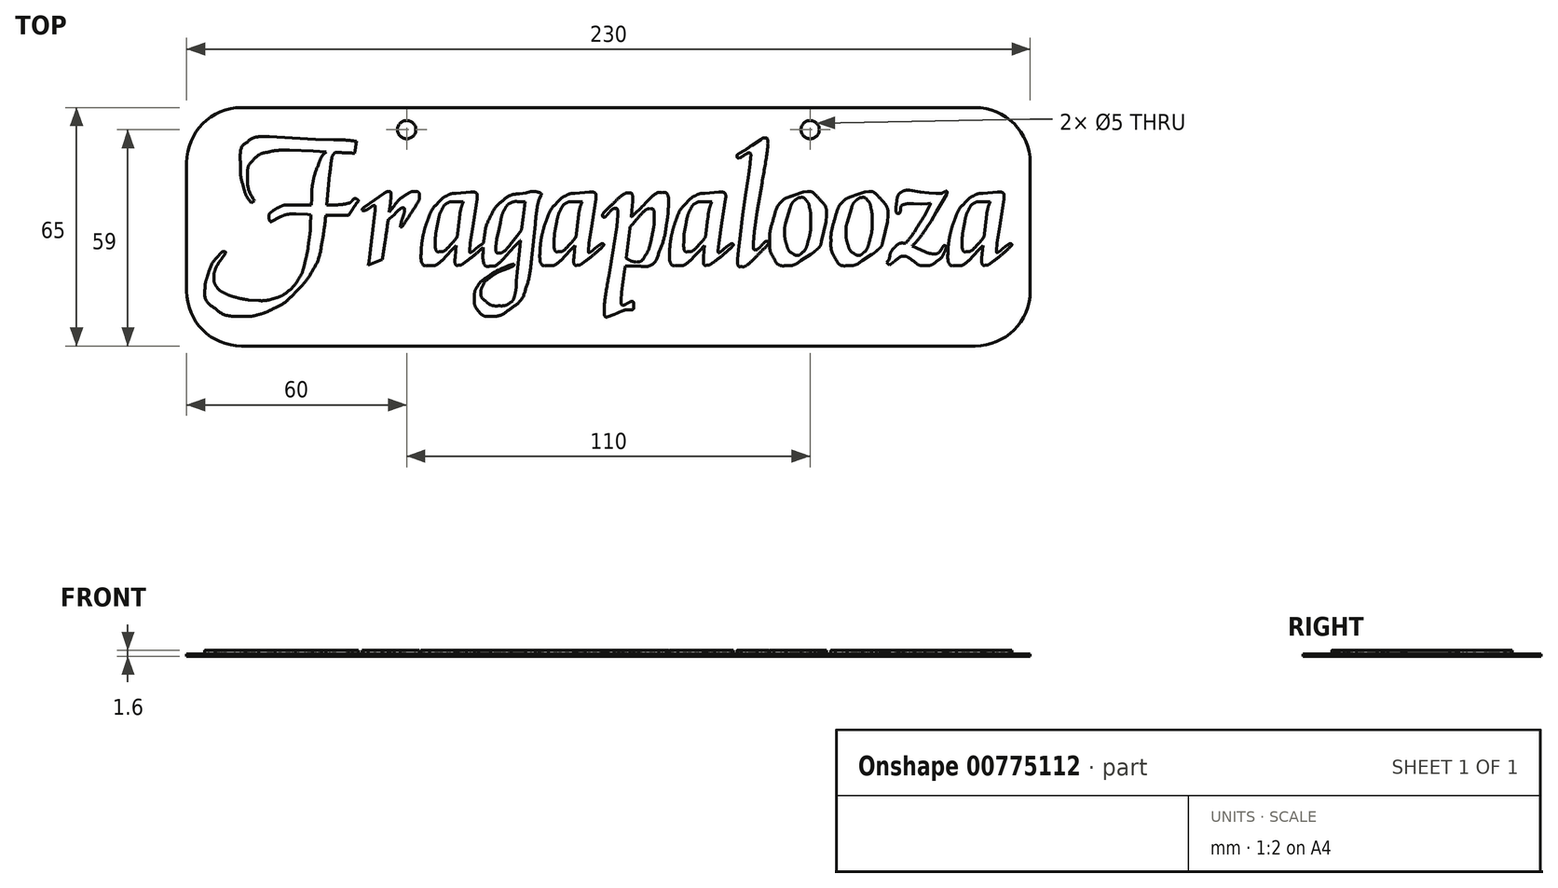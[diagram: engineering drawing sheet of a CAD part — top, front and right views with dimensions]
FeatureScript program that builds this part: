
annotation { "Feature Type Name" : "Feature", "Feature Type Description" : "" }
export const myFeature = defineFeature(function(context is Context, id is Id, definition is map)
    precondition{}
    {
        {
            var Q0;
            Q0=qCreatedBy(makeId("Top.planeOp"),FACE);
            var sketch = newSketch(context, id + "F0", { "sketchPlane" : qUnion([Q0])});
            skLineSegment(sketch, "E0.bottom", {"start": v(-100, 32.5) * mm, "end": v(100, 32.5) * mm});
            skLineSegment(sketch, "E0.top", {"start": v(-100, -32.5) * mm, "end": v(100, -32.5) * mm});
            skLineSegment(sketch, "E0.left", {"start": v(-115, 17.5) * mm, "end": v(-115, -17.5) * mm});
            skLineSegment(sketch, "E0.right", {"start": v(115, 17.5) * mm, "end": v(115, -17.5) * mm});
            skPoint(sketch, "E0.middle", {"position": v(0, 0) * mm});
            skPoint(sketch, "E1.visualSharp", {"position": v(-115, 32.5) * mm});
            skArc(sketch, "E1.filletArc", {"start": v(-100, 32.5) * mm, "mid": v(-110.6, 28.1) * mm, "end": v(-115, 17.5) * mm});
            skPoint(sketch, "E2.visualSharp", {"position": v(115, 32.5) * mm});
            skArc(sketch, "E2.filletArc", {"start": v(115, 17.5) * mm, "mid": v(110.6, 28.1) * mm, "end": v(100, 32.5) * mm});
            skPoint(sketch, "E3.visualSharp", {"position": v(115, -32.5) * mm});
            skArc(sketch, "E3.filletArc", {"start": v(100, -32.5) * mm, "mid": v(110.6, -28.1) * mm, "end": v(115, -17.5) * mm});
            skPoint(sketch, "E4.visualSharp", {"position": v(-115, -32.5) * mm});
            skArc(sketch, "E4.filletArc", {"start": v(-115, -17.5) * mm, "mid": v(-110.6, -28.1) * mm, "end": v(-100, -32.5) * mm});
            skCircle(sketch, "E5", {"center": v(-55, 26.5) * mm, "radius": 2.5 * mm});
            skCircle(sketch, "E6", {"center": v(55, 26.5) * mm, "radius": 2.5 * mm});
            skLineSegment(sketch, "E7", {"start": v(-55, 26.5) * mm, "end": v(0, 26.5) * mm, "construction": true});
            skLineSegment(sketch, "E8", {"start": v(0, 26.5) * mm, "end": v(55, 26.5) * mm, "construction": true});
            skSolve(sketch);
        }
        {
            var Q0;
            Q0=makeQuery(id+"F0.imprint","IMPRINT",FACE,{"disambiguationData":[TD([[makeQuery(id+"F0.imprint","IMPRINT",EDGE,{"derivedFrom":sQuery(id+"F0.wireOp",EDGE,"E0.bottom")}),-1.0]])]});
            extrude(context, id + "F1", {"entities" : qUnion([Q0]), "depth" : .6 * mm, "offsetDistance" : 25 * mm});
        }
        {
            var Q0;
            Q0=makeQuery(id+"F1.opExtrude","CAP_FACE",FACE,{"disambiguationData":[OSD([sQuery(id+"F0.wireOp",EDGE,"E0.bottom"),sQuery(id+"F0.wireOp",EDGE,"E0.top"),sQuery(id+"F0.wireOp",EDGE,"E0.left"),sQuery(id+"F0.wireOp",EDGE,"E0.right")])],"isStart":false});
            var sketch = newSketch(context, id + "F2", { "sketchPlane" : qUnion([Q0])});
            skLineSegment(sketch, "E9", {"start": v(-92.11, 1.33) * mm, "end": v(-89.44, 2.74) * mm});
            skLineSegment(sketch, "E10", {"start": v(-85.15, 3.5) * mm, "end": v(-82, 3.36) * mm});
            skLineSegment(sketch, "E11", {"start": v(-82, 3.36) * mm, "end": v(-78.73, 3.18) * mm});
            skLineSegment(sketch, "E12", {"start": v(-78.73, 3.18) * mm, "end": v(-70.78, 3.18) * mm});
            skLineSegment(sketch, "E13", {"start": v(-70.78, 3.18) * mm, "end": v(-69.8, 4.65) * mm});
            skLineSegment(sketch, "E14", {"start": v(-68.12, 7.04) * mm, "end": v(-68.17, 7.2) * mm});
            skLineSegment(sketch, "E15", {"start": v(-77.15, 5.95) * mm, "end": v(-80.41, 5.95) * mm});
            skLineSegment(sketch, "E16", {"start": v(-80.41, 5.95) * mm, "end": v(-84.55, 5.95) * mm});
            skLineSegment(sketch, "E17", {"start": v(-84.55, 5.95) * mm, "end": v(-87.87, 5.95) * mm});
            skLineSegment(sketch, "E18", {"start": v(-86.92, 20.9) * mm, "end": v(-80.51, 20.63) * mm});
            skLineSegment(sketch, "E19", {"start": v(-80.51, 20.63) * mm, "end": v(-74.61, 20.25) * mm});
            skLineSegment(sketch, "E20", {"start": v(-69.22, 20.03) * mm, "end": v(-68.67, 23.34) * mm});
            skLineSegment(sketch, "E21", {"start": v(-74.87, 23.74) * mm, "end": v(-79.85, 23.85) * mm});
            skLineSegment(sketch, "E22", {"start": v(-79.85, 23.85) * mm, "end": v(-86.2, 24.25) * mm});
            skLineSegment(sketch, "E23", {"start": v(-86.2, 24.25) * mm, "end": v(-92.4, 24.56) * mm});
            skLineSegment(sketch, "E24", {"start": v(-97.4, 6.61) * mm, "end": v(-96.48, 7.12) * mm});
            skLineSegment(sketch, "E25", {"start": v(-76.95, 4.81) * mm, "end": v(-75.99, 14.38) * mm});
            skLineSegment(sketch, "E26", {"start": v(-75.12, 19.57) * mm, "end": v(-74.46, 20.29) * mm});
            skLineSegment(sketch, "E27", {"start": v(-74.15, 21.15) * mm, "end": v(-75.12, 20.95) * mm});
            skLineSegment(sketch, "E28", {"start": v(-80.92, 7.78) * mm, "end": v(-81.22, 0.56) * mm});
            skLineSegment(sketch, "E29", {"start": v(-95.36, -20.13) * mm, "end": v(-98.05, -19.93) * mm});
            skLineSegment(sketch, "E30", {"start": v(-105.53, -8.84) * mm, "end": v(-104.56, -7.57) * mm});
            skLineSegment(sketch, "E31", {"start": v(-104.56, -7.57) * mm, "end": v(-104.4, -7.17) * mm});
            skLineSegment(sketch, "E32", {"start": v(-59.4, 6.55) * mm, "end": v(-59.26, 8.23) * mm});
            skLineSegment(sketch, "E33", {"start": v(-61.19, 9.15) * mm, "end": v(-63.78, 7.35) * mm});
            skLineSegment(sketch, "E34", {"start": v(-63.78, 7.35) * mm, "end": v(-66.68, 5.3) * mm});
            skLineSegment(sketch, "E35", {"start": v(-67.09, 4.53) * mm, "end": v(-66.88, 4.42) * mm});
            skLineSegment(sketch, "E36", {"start": v(-66.88, 4.42) * mm, "end": v(-66.58, 4.47) * mm});
            skLineSegment(sketch, "E37", {"start": v(-66.58, 4.47) * mm, "end": v(-66.27, 4.53) * mm});
            skLineSegment(sketch, "E38", {"start": v(-63.58, 4.53) * mm, "end": v(-64.6, -3.97) * mm});
            skLineSegment(sketch, "E39", {"start": v(-64.6, -3.97) * mm, "end": v(-65.26, -9.46) * mm});
            skLineSegment(sketch, "E40", {"start": v(-65.51, -10.42) * mm, "end": v(-61.65, -8.94) * mm});
            skLineSegment(sketch, "E41", {"start": v(-58.44, 5.7) * mm, "end": v(-60.27, 3.36) * mm});
            skLineSegment(sketch, "E42", {"start": v(-59.66, 2.24) * mm, "end": v(-58.44, 3.3) * mm});
            skLineSegment(sketch, "E43", {"start": v(-39.33, 6.88) * mm, "end": v(-38, 6.88) * mm});
            skLineSegment(sketch, "E44", {"start": v(-38, 6.88) * mm, "end": v(-37.04, 7.08) * mm});
            skLineSegment(sketch, "E45", {"start": v(-37.6, 9.47) * mm, "end": v(-41.46, 9.11) * mm});
            skLineSegment(sketch, "E46", {"start": v(-42.99, -6.63) * mm, "end": v(-41.26, -4.74) * mm});
            skLineSegment(sketch, "E47", {"start": v(-39.63, -0.7) * mm, "end": v(-40.8, -2.13) * mm});
            skLineSegment(sketch, "E48", {"start": v(-42.12, 6.88) * mm, "end": v(-40.9, 6.88) * mm});
            skLineSegment(sketch, "E49", {"start": v(-40.9, 6.88) * mm, "end": v(-39.33, 6.88) * mm});
            skLineSegment(sketch, "E50", {"start": v(-40.59, 2.44) * mm, "end": v(-41.18, -1.98) * mm});
            skLineSegment(sketch, "E51", {"start": v(-41.18, -1.98) * mm, "end": v(-41.68, -6.2) * mm});
            skLineSegment(sketch, "E52", {"start": v(-41.68, -6.2) * mm, "end": v(-41.82, -8.6) * mm});
            skLineSegment(sketch, "E53", {"start": v(-36.58, -6.36) * mm, "end": v(-37.65, -7.12) * mm});
            skLineSegment(sketch, "E54", {"start": v(-37.85, -6.5) * mm, "end": v(-37.65, -4.42) * mm});
            skLineSegment(sketch, "E55", {"start": v(-37.65, -4.42) * mm, "end": v(-36.8, 1.02) * mm});
            skLineSegment(sketch, "E56", {"start": v(-36.8, 1.02) * mm, "end": v(-35.78, 7.58) * mm});
            skLineSegment(sketch, "E57", {"start": v(-21.58, 6.88) * mm, "end": v(-20.28, 6.88) * mm});
            skLineSegment(sketch, "E58", {"start": v(-20.28, 6.88) * mm, "end": v(-19.33, 7.12) * mm});
            skLineSegment(sketch, "E59", {"start": v(-18.74, 7.75) * mm, "end": v(-18.33, 8.63) * mm});
            skLineSegment(sketch, "E60", {"start": v(-19.85, 9.65) * mm, "end": v(-21.12, 9.65) * mm});
            skLineSegment(sketch, "E61", {"start": v(-21.12, 9.65) * mm, "end": v(-22.45, 9.2) * mm});
            skLineSegment(sketch, "E62", {"start": v(-22.45, 9.2) * mm, "end": v(-24.23, 9) * mm});
            skLineSegment(sketch, "E63", {"start": v(-27.23, -7.1) * mm, "end": v(-25.1, -4.86) * mm});
            skLineSegment(sketch, "E64", {"start": v(-23.06, -0.05) * mm, "end": v(-24.84, -2.4) * mm});
            skLineSegment(sketch, "E65", {"start": v(-24.84, -2.4) * mm, "end": v(-26.87, -5.02) * mm});
            skLineSegment(sketch, "E66", {"start": v(-30.68, -5.5) * mm, "end": v(-30.48, -3.38) * mm});
            skLineSegment(sketch, "E67", {"start": v(-30.48, -3.38) * mm, "end": v(-29.87, -0.6) * mm});
            skLineSegment(sketch, "E68", {"start": v(-29.87, -0.6) * mm, "end": v(-29.46, 1.1) * mm});
            skLineSegment(sketch, "E69", {"start": v(-24.73, 6.88) * mm, "end": v(-23.26, 6.88) * mm});
            skLineSegment(sketch, "E70", {"start": v(-23.26, 6.88) * mm, "end": v(-21.58, 6.88) * mm});
            skLineSegment(sketch, "E71", {"start": v(-22.45, 8.37) * mm, "end": v(-23.27, 2.78) * mm});
            skLineSegment(sketch, "E72", {"start": v(-23.27, 2.78) * mm, "end": v(-24.16, -5.26) * mm});
            skLineSegment(sketch, "E73", {"start": v(-24.16, -5.26) * mm, "end": v(-24.77, -11.16) * mm});
            skLineSegment(sketch, "E74", {"start": v(-24.77, -11.16) * mm, "end": v(-25.1, -14.82) * mm});
            skLineSegment(sketch, "E75", {"start": v(-29.77, -12.22) * mm, "end": v(-27.07, -11.15) * mm});
            skLineSegment(sketch, "E76", {"start": v(-25.6, -10.4) * mm, "end": v(-25.7, -10.24) * mm});
            skLineSegment(sketch, "E77", {"start": v(-20.92, -8.56) * mm, "end": v(-19.96, 0.74) * mm});
            skLineSegment(sketch, "E78", {"start": v(-6.94, 6.88) * mm, "end": v(-5.62, 6.88) * mm});
            skLineSegment(sketch, "E79", {"start": v(-5.62, 6.88) * mm, "end": v(-4.65, 7.08) * mm});
            skLineSegment(sketch, "E80", {"start": v(-5.21, 9.47) * mm, "end": v(-9.08, 9.11) * mm});
            skLineSegment(sketch, "E81", {"start": v(-10.6, -6.63) * mm, "end": v(-8.87, -4.74) * mm});
            skLineSegment(sketch, "E82", {"start": v(-7.24, -0.7) * mm, "end": v(-8.41, -2.13) * mm});
            skLineSegment(sketch, "E83", {"start": v(-9.74, 6.88) * mm, "end": v(-8.52, 6.88) * mm});
            skLineSegment(sketch, "E84", {"start": v(-8.52, 6.88) * mm, "end": v(-6.94, 6.88) * mm});
            skLineSegment(sketch, "E85", {"start": v(-8.2, 2.44) * mm, "end": v(-8.79, -1.98) * mm});
            skLineSegment(sketch, "E86", {"start": v(-8.79, -1.98) * mm, "end": v(-9.3, -6.2) * mm});
            skLineSegment(sketch, "E87", {"start": v(-9.3, -6.2) * mm, "end": v(-9.43, -8.6) * mm});
            skLineSegment(sketch, "E88", {"start": v(-4.2, -6.36) * mm, "end": v(-5.26, -7.12) * mm});
            skLineSegment(sketch, "E89", {"start": v(-5.47, -6.5) * mm, "end": v(-5.26, -4.42) * mm});
            skLineSegment(sketch, "E90", {"start": v(-5.26, -4.42) * mm, "end": v(-4.4, 1.02) * mm});
            skLineSegment(sketch, "E91", {"start": v(-4.4, 1.02) * mm, "end": v(-3.4, 7.58) * mm});
            skLineSegment(sketch, "E92", {"start": v(2.52, 3.3) * mm, "end": v(2.26, 0.05) * mm});
            skLineSegment(sketch, "E93", {"start": v(2.26, 0.05) * mm, "end": v(1.43, -5.54) * mm});
            skLineSegment(sketch, "E94", {"start": v(1.43, -5.54) * mm, "end": v(0.12, -13.32) * mm});
            skLineSegment(sketch, "E95", {"start": v(-0.18, -24.56) * mm, "end": v(1.5, -23.95) * mm});
            skLineSegment(sketch, "E96", {"start": v(3.48, -20.03) * mm, "end": v(3.59, -17.84) * mm});
            skLineSegment(sketch, "E97", {"start": v(3.59, -17.84) * mm, "end": v(4.37, -12.25) * mm});
            skLineSegment(sketch, "E98", {"start": v(4.37, -12.25) * mm, "end": v(5.35, -4.47) * mm});
            skLineSegment(sketch, "E99", {"start": v(5.35, -4.47) * mm, "end": v(5.85, -0.35) * mm});
            skLineSegment(sketch, "E100", {"start": v(5.85, -0.35) * mm, "end": v(6.43, 4.42) * mm});
            skLineSegment(sketch, "E101", {"start": v(6.43, 4.42) * mm, "end": v(6.58, 6.97) * mm});
            skLineSegment(sketch, "E102", {"start": v(3.43, -8.96) * mm, "end": v(3.28, -9.48) * mm});
            skLineSegment(sketch, "E103", {"start": v(2.82, -10.68) * mm, "end": v(2.97, -10.82) * mm});
            skLineSegment(sketch, "E104", {"start": v(2.97, -10.82) * mm, "end": v(3.17, -10.9) * mm});
            skLineSegment(sketch, "E105", {"start": v(3.17, -10.9) * mm, "end": v(4.2, -10.7) * mm});
            skLineSegment(sketch, "E106", {"start": v(4.2, -10.7) * mm, "end": v(6.03, -10.7) * mm});
            skLineSegment(sketch, "E107", {"start": v(6.03, -10.7) * mm, "end": v(8.28, -10.7) * mm});
            skLineSegment(sketch, "E108", {"start": v(8.97, 5.25) * mm, "end": v(7.2, 3.56) * mm});
            skLineSegment(sketch, "E109", {"start": v(28.4, 6.88) * mm, "end": v(29.72, 6.88) * mm});
            skLineSegment(sketch, "E110", {"start": v(29.72, 6.88) * mm, "end": v(30.68, 7.08) * mm});
            skLineSegment(sketch, "E111", {"start": v(30.13, 9.47) * mm, "end": v(26.26, 9.11) * mm});
            skLineSegment(sketch, "E112", {"start": v(24.74, -6.63) * mm, "end": v(26.46, -4.74) * mm});
            skLineSegment(sketch, "E113", {"start": v(28.1, -0.7) * mm, "end": v(26.92, -2.13) * mm});
            skLineSegment(sketch, "E114", {"start": v(25.6, 6.88) * mm, "end": v(26.82, 6.88) * mm});
            skLineSegment(sketch, "E115", {"start": v(26.82, 6.88) * mm, "end": v(28.4, 6.88) * mm});
            skLineSegment(sketch, "E116", {"start": v(27.14, 2.44) * mm, "end": v(26.55, -1.98) * mm});
            skLineSegment(sketch, "E117", {"start": v(26.55, -1.98) * mm, "end": v(26.04, -6.2) * mm});
            skLineSegment(sketch, "E118", {"start": v(26.04, -6.2) * mm, "end": v(25.9, -8.6) * mm});
            skLineSegment(sketch, "E119", {"start": v(31.14, -6.36) * mm, "end": v(30.07, -7.12) * mm});
            skLineSegment(sketch, "E120", {"start": v(29.87, -6.5) * mm, "end": v(30.07, -4.42) * mm});
            skLineSegment(sketch, "E121", {"start": v(30.07, -4.42) * mm, "end": v(30.93, 1.02) * mm});
            skLineSegment(sketch, "E122", {"start": v(30.93, 1.02) * mm, "end": v(31.94, 7.58) * mm});
            skLineSegment(sketch, "E123", {"start": v(39.48, -4.47) * mm, "end": v(39.73, -1.27) * mm});
            skLineSegment(sketch, "E124", {"start": v(39.73, -1.27) * mm, "end": v(40.5, 4.12) * mm});
            skLineSegment(sketch, "E125", {"start": v(40.5, 4.12) * mm, "end": v(41.88, 12.05) * mm});
            skLineSegment(sketch, "E126", {"start": v(41.67, 23.9) * mm, "end": v(39.12, 22.22) * mm});
            skLineSegment(sketch, "E127", {"start": v(35.46, 18.76) * mm, "end": v(36.07, 18.97) * mm});
            skLineSegment(sketch, "E128", {"start": v(38.82, 19.07) * mm, "end": v(38.66, 17.14) * mm});
            skLineSegment(sketch, "E129", {"start": v(38.66, 17.14) * mm, "end": v(38.12, 13.47) * mm});
            skLineSegment(sketch, "E130", {"start": v(38.12, 13.47) * mm, "end": v(37.37, 8.65) * mm});
            skLineSegment(sketch, "E131", {"start": v(37.37, 8.65) * mm, "end": v(36.65, 3.26) * mm});
            skLineSegment(sketch, "E132", {"start": v(36.65, 3.26) * mm, "end": v(35.93, -2.13) * mm});
            skLineSegment(sketch, "E133", {"start": v(35.93, -2.13) * mm, "end": v(35.41, -6.36) * mm});
            skLineSegment(sketch, "E134", {"start": v(35.41, -6.36) * mm, "end": v(35.26, -8.8) * mm});
            skLineSegment(sketch, "E135", {"start": v(52.5, -9.2) * mm, "end": v(55.09, -7.53) * mm});
            skLineSegment(sketch, "E136", {"start": v(58.09, -3.98) * mm, "end": v(58.7, -1.24) * mm});
            skLineSegment(sketch, "E137", {"start": v(58.7, -1.24) * mm, "end": v(59.3, 1.34) * mm});
            skLineSegment(sketch, "E138", {"start": v(59.3, 1.34) * mm, "end": v(59.46, 3.12) * mm});
            skLineSegment(sketch, "E139", {"start": v(54.28, 9.6) * mm, "end": v(53.1, 9.46) * mm});
            skLineSegment(sketch, "E140", {"start": v(53.1, 9.46) * mm, "end": v(50.51, 8.6) * mm});
            skLineSegment(sketch, "E141", {"start": v(48.33, 0.97) * mm, "end": v(49.55, 5.19) * mm});
            skLineSegment(sketch, "E142", {"start": v(69.22, -9.2) * mm, "end": v(71.82, -7.53) * mm});
            skLineSegment(sketch, "E143", {"start": v(74.82, -3.98) * mm, "end": v(75.43, -1.24) * mm});
            skLineSegment(sketch, "E144", {"start": v(75.43, -1.24) * mm, "end": v(76.04, 1.34) * mm});
            skLineSegment(sketch, "E145", {"start": v(76.04, 1.34) * mm, "end": v(76.19, 3.12) * mm});
            skLineSegment(sketch, "E146", {"start": v(71, 9.6) * mm, "end": v(69.83, 9.46) * mm});
            skLineSegment(sketch, "E147", {"start": v(69.83, 9.46) * mm, "end": v(67.24, 8.6) * mm});
            skLineSegment(sketch, "E148", {"start": v(65.05, 0.97) * mm, "end": v(66.27, 5.19) * mm});
            skLineSegment(sketch, "E149", {"start": v(83.16, 6.3) * mm, "end": v(85.19, 6.2) * mm});
            skLineSegment(sketch, "E150", {"start": v(85.19, 6.2) * mm, "end": v(86.97, 6.3) * mm});
            skLineSegment(sketch, "E151", {"start": v(86.97, 6.3) * mm, "end": v(87.83, 6.4) * mm});
            skLineSegment(sketch, "E152", {"start": v(75.88, -9.6) * mm, "end": v(76.65, -10.42) * mm});
            skLineSegment(sketch, "E153", {"start": v(86.66, -0.4) * mm, "end": v(87.98, 1.68) * mm});
            skLineSegment(sketch, "E154", {"start": v(87.98, 1.68) * mm, "end": v(89.46, 4.17) * mm});
            skLineSegment(sketch, "E155", {"start": v(89.46, 4.17) * mm, "end": v(90.93, 6.76) * mm});
            skLineSegment(sketch, "E156", {"start": v(90.93, 6.76) * mm, "end": v(92.2, 8.9) * mm});
            skLineSegment(sketch, "E157", {"start": v(91.95, 9.71) * mm, "end": v(91.54, 9.56) * mm});
            skLineSegment(sketch, "E158", {"start": v(89.3, 9.1) * mm, "end": v(87.38, 9.2) * mm});
            skLineSegment(sketch, "E159", {"start": v(87.38, 9.2) * mm, "end": v(84.99, 9.5) * mm});
            skLineSegment(sketch, "E160", {"start": v(84.99, 9.5) * mm, "end": v(82.04, 9.97) * mm});
            skLineSegment(sketch, "E161", {"start": v(78.63, 7.07) * mm, "end": v(78.43, 5.34) * mm});
            skLineSegment(sketch, "E162", {"start": v(75.99, -9.56) * mm, "end": v(76.34, -10.02) * mm});
            skLineSegment(sketch, "E163", {"start": v(76.8, -10.27) * mm, "end": v(79.09, -8.5) * mm});
            skLineSegment(sketch, "E164", {"start": v(86.56, -6.92) * mm, "end": v(83.97, -5.75) * mm});
            skLineSegment(sketch, "E165", {"start": v(83.97, -5.75) * mm, "end": v(81.58, -4.63) * mm});
            skLineSegment(sketch, "E166", {"start": v(76.7, -7.98) * mm, "end": v(76.6, -8.54) * mm});
            skLineSegment(sketch, "E167", {"start": v(76.6, -8.54) * mm, "end": v(76.44, -9.05) * mm});
            skLineSegment(sketch, "E168", {"start": v(76.44, -9.05) * mm, "end": v(75.99, -9.56) * mm});
            skLineSegment(sketch, "E169", {"start": v(104.3, 6.88) * mm, "end": v(105.63, 6.88) * mm});
            skLineSegment(sketch, "E170", {"start": v(105.63, 6.88) * mm, "end": v(106.6, 7.08) * mm});
            skLineSegment(sketch, "E171", {"start": v(106.03, 9.47) * mm, "end": v(102.17, 9.11) * mm});
            skLineSegment(sketch, "E172", {"start": v(100.65, -6.63) * mm, "end": v(102.37, -4.74) * mm});
            skLineSegment(sketch, "E173", {"start": v(104, -0.7) * mm, "end": v(102.83, -2.13) * mm});
            skLineSegment(sketch, "E174", {"start": v(101.5, 6.88) * mm, "end": v(102.73, 6.88) * mm});
            skLineSegment(sketch, "E175", {"start": v(102.73, 6.88) * mm, "end": v(104.3, 6.88) * mm});
            skLineSegment(sketch, "E176", {"start": v(103.05, 2.44) * mm, "end": v(102.45, -1.98) * mm});
            skLineSegment(sketch, "E177", {"start": v(102.45, -1.98) * mm, "end": v(101.95, -6.2) * mm});
            skLineSegment(sketch, "E178", {"start": v(101.95, -6.2) * mm, "end": v(101.81, -8.6) * mm});
            skLineSegment(sketch, "E179", {"start": v(107.05, -6.36) * mm, "end": v(105.98, -7.12) * mm});
            skLineSegment(sketch, "E180", {"start": v(105.78, -6.5) * mm, "end": v(105.98, -4.42) * mm});
            skLineSegment(sketch, "E181", {"start": v(105.98, -4.42) * mm, "end": v(106.84, 1.02) * mm});
            skLineSegment(sketch, "E182", {"start": v(106.84, 1.02) * mm, "end": v(107.85, 7.58) * mm});
            skFitSpline(sketch, "E183", {"points": [v(-92.55, 2.47) * mm, v(-92.55, 2.22) * mm, v(-92.4, 1.83) * mm, v(-92.11, 1.33) * mm]});
            skFitSpline(sketch, "E184", {"points": [v(-89.44, 2.74) * mm, v(-88.14, 3.25) * mm, v(-86.7, 3.5) * mm, v(-85.15, 3.5) * mm]});
            skFitSpline(sketch, "E185", {"points": [v(-69.8, 4.65) * mm, v(-69.15, 5.73) * mm, v(-68.6, 6.53) * mm, v(-68.12, 7.04) * mm]});
            skFitSpline(sketch, "E186", {"points": [v(-68.17, 7.2) * mm, v(-68.2, 7.27) * mm, v(-68.32, 7.37) * mm, v(-68.5, 7.5) * mm]});
            skFitSpline(sketch, "E187", {"points": [v(-68.5, 7.5) * mm, v(-68.68, 7.63) * mm, v(-68.84, 7.7) * mm, v(-68.99, 7.7) * mm]});
            skFitSpline(sketch, "E188", {"points": [v(-68.99, 7.7) * mm, v(-69.28, 7.7) * mm, v(-69.58, 7.51) * mm, v(-69.89, 7.15) * mm]});
            skFitSpline(sketch, "E189", {"points": [v(-69.89, 7.15) * mm, v(-70.2, 6.78) * mm, v(-70.5, 6.55) * mm, v(-70.78, 6.44) * mm]});
            skFitSpline(sketch, "E190", {"points": [v(-70.78, 6.44) * mm, v(-72.7, 6.12) * mm, v(-74.83, 5.95) * mm, v(-77.15, 5.95) * mm]});
            skFitSpline(sketch, "E191", {"points": [v(-87.87, 5.95) * mm, v(-88.27, 5.95) * mm, v(-88.88, 5.77) * mm, v(-89.72, 5.4) * mm]});
            skFitSpline(sketch, "E192", {"points": [v(-89.72, 5.4) * mm, v(-90.62, 4.93) * mm, v(-91.33, 4.5) * mm, v(-91.84, 4.1) * mm]});
            skFitSpline(sketch, "E193", {"points": [v(-91.84, 4.1) * mm, v(-92.31, 3.74) * mm, v(-92.55, 3.2) * mm, v(-92.55, 2.47) * mm]});
            skFitSpline(sketch, "E194", {"points": [v(-96.48, 7.12) * mm, v(-97.73, 9.19) * mm, v(-98.36, 11.47) * mm, v(-98.36, 13.98) * mm]});
            skFitSpline(sketch, "E195", {"points": [v(-98.36, 13.98) * mm, v(-98.36, 15.71) * mm, v(-97.85, 17.12) * mm, v(-96.83, 18.2) * mm]});
            skFitSpline(sketch, "E196", {"points": [v(-96.83, 18.2) * mm, v(-95.81, 19.29) * mm, v(-94.5, 20) * mm, v(-92.9, 20.36) * mm]});
            skFitSpline(sketch, "E197", {"points": [v(-92.9, 20.36) * mm, v(-91.28, 20.72) * mm, v(-89.29, 20.9) * mm, v(-86.92, 20.9) * mm]});
            skFitSpline(sketch, "E198", {"points": [v(-74.61, 20.25) * mm, v(-73.53, 20.25) * mm, v(-72.48, 20.23) * mm, v(-71.46, 20.19) * mm]});
            skFitSpline(sketch, "E199", {"points": [v(-71.46, 20.19) * mm, v(-70.44, 20.14) * mm, v(-69.7, 20.1) * mm, v(-69.22, 20.03) * mm]});
            skFitSpline(sketch, "E200", {"points": [v(-68.67, 23.34) * mm, v(-71.04, 23.6) * mm, v(-73.1, 23.74) * mm, v(-74.87, 23.74) * mm]});
            skFitSpline(sketch, "E201", {"points": [v(-92.4, 24.56) * mm, v(-95.26, 24.56) * mm, v(-97.27, 24.07) * mm, v(-98.46, 23.08) * mm]});
            skFitSpline(sketch, "E202", {"points": [v(-98.46, 23.08) * mm, v(-99.71, 22.17) * mm, v(-100.34, 20.32) * mm, v(-100.34, 17.54) * mm]});
            skFitSpline(sketch, "E203", {"points": [v(-100.34, 17.54) * mm, v(-100.34, 15.1) * mm, v(-100.08, 12.96) * mm, v(-99.55, 11.1) * mm]});
            skFitSpline(sketch, "E204", {"points": [v(-99.55, 11.1) * mm, v(-99.03, 9.26) * mm, v(-98.3, 7.76) * mm, v(-97.4, 6.61) * mm]});
            skFitSpline(sketch, "E205", {"points": [v(-106.72, -8.36) * mm, v(-107.69, -9.46) * mm, v(-108.47, -10.92) * mm, v(-109.08, -12.74) * mm]});
            skFitSpline(sketch, "E206", {"points": [v(-109.08, -12.74) * mm, v(-109.7, -14.57) * mm, v(-110, -15.94) * mm, v(-110, -16.85) * mm]});
            skFitSpline(sketch, "E207", {"points": [v(-110, -16.85) * mm, v(-110, -19.05) * mm, v(-109.06, -20.86) * mm, v(-107.18, -22.28) * mm]});
            skFitSpline(sketch, "E208", {"points": [v(-107.18, -22.28) * mm, v(-105.3, -23.7) * mm, v(-102.53, -24.4) * mm, v(-98.87, -24.4) * mm]});
            skFitSpline(sketch, "E209", {"points": [v(-98.87, -24.4) * mm, v(-97.68, -24.4) * mm, v(-96.5, -24.24) * mm, v(-95.3, -23.9) * mm]});
            skFitSpline(sketch, "E210", {"points": [v(-95.3, -23.9) * mm, v(-94.12, -23.56) * mm, v(-92.65, -22.96) * mm, v(-90.88, -22.09) * mm]});
            skFitSpline(sketch, "E211", {"points": [v(-90.88, -22.09) * mm, v(-89.12, -21.22) * mm, v(-87.26, -19.8) * mm, v(-85.29, -17.79) * mm]});
            skFitSpline(sketch, "E212", {"points": [v(-85.29, -17.79) * mm, v(-83.32, -15.79) * mm, v(-81.77, -13.8) * mm, v(-80.64, -11.83) * mm]});
            skFitSpline(sketch, "E213", {"points": [v(-80.64, -11.83) * mm, v(-79.5, -9.87) * mm, v(-78.68, -7.46) * mm, v(-78.17, -4.63) * mm]});
            skFitSpline(sketch, "E214", {"points": [v(-78.17, -4.63) * mm, v(-77.66, -1.8) * mm, v(-77.26, 1.35) * mm, v(-76.95, 4.81) * mm]});
            skFitSpline(sketch, "E215", {"points": [v(-75.99, 14.38) * mm, v(-75.61, 17.44) * mm, v(-75.32, 19.17) * mm, v(-75.12, 19.57) * mm]});
            skFitSpline(sketch, "E216", {"points": [v(-74.46, 20.29) * mm, v(-74.22, 20.51) * mm, v(-74.08, 20.67) * mm, v(-74.03, 20.77) * mm]});
            skFitSpline(sketch, "E217", {"points": [v(-74.03, 20.77) * mm, v(-73.98, 20.86) * mm, v(-73.93, 20.96) * mm, v(-73.9, 21.06) * mm]});
            skFitSpline(sketch, "E218", {"points": [v(-73.9, 21.06) * mm, v(-74, 21.12) * mm, v(-74.09, 21.15) * mm, v(-74.15, 21.15) * mm]});
            skFitSpline(sketch, "E219", {"points": [v(-75.12, 20.95) * mm, v(-76.88, 20.44) * mm, v(-78.16, 19.2) * mm, v(-78.96, 17.24) * mm]});
            skFitSpline(sketch, "E220", {"points": [v(-78.96, 17.24) * mm, v(-79.76, 15.27) * mm, v(-80.28, 13.58) * mm, v(-80.54, 12.18) * mm]});
            skFitSpline(sketch, "E221", {"points": [v(-80.54, 12.18) * mm, v(-80.8, 10.77) * mm, v(-80.92, 9.3) * mm, v(-80.92, 7.78) * mm]});
            skFitSpline(sketch, "E222", {"points": [v(-81.22, 0.56) * mm, v(-81.22, -0.19) * mm, v(-81.26, -0.86) * mm, v(-81.32, -1.45) * mm]});
            skFitSpline(sketch, "E223", {"points": [v(-81.32, -1.45) * mm, v(-81.4, -2.04) * mm, v(-81.53, -2.97) * mm, v(-81.73, -4.22) * mm]});
            skFitSpline(sketch, "E224", {"points": [v(-81.73, -4.22) * mm, v(-81.93, -5.95) * mm, v(-82.26, -7.75) * mm, v(-82.72, -9.64) * mm]});
            skFitSpline(sketch, "E225", {"points": [v(-82.72, -9.64) * mm, v(-83.18, -11.52) * mm, v(-83.8, -13.1) * mm, v(-84.6, -14.39) * mm]});
            skFitSpline(sketch, "E226", {"points": [v(-84.6, -14.39) * mm, v(-85.4, -15.68) * mm, v(-86.36, -16.78) * mm, v(-87.48, -17.7) * mm]});
            skFitSpline(sketch, "E227", {"points": [v(-87.48, -17.7) * mm, v(-88.6, -18.5) * mm, v(-89.83, -19.12) * mm, v(-91.19, -19.52) * mm]});
            skFitSpline(sketch, "E228", {"points": [v(-91.19, -19.52) * mm, v(-92.54, -19.93) * mm, v(-93.93, -20.13) * mm, v(-95.36, -20.13) * mm]});
            skFitSpline(sketch, "E229", {"points": [v(-98.05, -19.93) * mm, v(-99.58, -19.7) * mm, v(-100.87, -19.42) * mm, v(-101.94, -19.12) * mm]});
            skFitSpline(sketch, "E230", {"points": [v(-101.94, -19.12) * mm, v(-103, -18.82) * mm, v(-103.97, -18.44) * mm, v(-104.84, -17.98) * mm]});
            skFitSpline(sketch, "E231", {"points": [v(-104.84, -17.98) * mm, v(-105.7, -17.53) * mm, v(-106.37, -16.94) * mm, v(-106.85, -16.23) * mm]});
            skFitSpline(sketch, "E232", {"points": [v(-106.85, -16.23) * mm, v(-107.32, -15.53) * mm, v(-107.56, -14.7) * mm, v(-107.56, -13.75) * mm]});
            skFitSpline(sketch, "E233", {"points": [v(-107.56, -13.75) * mm, v(-107.56, -13.11) * mm, v(-107.46, -12.48) * mm, v(-107.25, -11.85) * mm]});
            skFitSpline(sketch, "E234", {"points": [v(-107.25, -11.85) * mm, v(-107.05, -11.23) * mm, v(-106.8, -10.7) * mm, v(-106.5, -10.26) * mm]});
            skFitSpline(sketch, "E235", {"points": [v(-106.5, -10.26) * mm, v(-106.36, -9.95) * mm, v(-106.23, -9.73) * mm, v(-106.11, -9.57) * mm]});
            skFitSpline(sketch, "E236", {"points": [v(-106.11, -9.57) * mm, v(-106, -9.42) * mm, v(-105.8, -9.18) * mm, v(-105.53, -8.84) * mm]});
            skFitSpline(sketch, "E237", {"points": [v(-104.4, -7.17) * mm, v(-104.4, -6.86) * mm, v(-104.58, -6.71) * mm, v(-104.92, -6.71) * mm]});
            skFitSpline(sketch, "E238", {"points": [v(-104.92, -6.71) * mm, v(-105.15, -6.71) * mm, v(-105.76, -7.26) * mm, v(-106.72, -8.36) * mm]});
            skFitSpline(sketch, "E239", {"points": [v(-60.96, -4.51) * mm, v(-60.74, -3.01) * mm, v(-60.22, 0.67) * mm, v(-59.4, 6.55) * mm]});
            skFitSpline(sketch, "E240", {"points": [v(-59.26, 8.23) * mm, v(-59.26, 9.15) * mm, v(-59.48, 9.6) * mm, v(-59.92, 9.6) * mm]});
            skFitSpline(sketch, "E241", {"points": [v(-59.92, 9.6) * mm, v(-60.26, 9.6) * mm, v(-60.68, 9.46) * mm, v(-61.19, 9.15) * mm]});
            skFitSpline(sketch, "E242", {"points": [v(-66.68, 5.3) * mm, v(-66.95, 5.1) * mm, v(-67.09, 4.83) * mm, v(-67.09, 4.53) * mm]});
            skFitSpline(sketch, "E243", {"points": [v(-66.27, 4.53) * mm, v(-66, 4.6) * mm, v(-65.59, 4.82) * mm, v(-65.03, 5.21) * mm]});
            skFitSpline(sketch, "E244", {"points": [v(-65.03, 5.21) * mm, v(-64.47, 5.6) * mm, v(-64.09, 5.8) * mm, v(-63.88, 5.8) * mm]});
            skFitSpline(sketch, "E245", {"points": [v(-63.88, 5.8) * mm, v(-63.68, 5.8) * mm, v(-63.58, 5.37) * mm, v(-63.58, 4.53) * mm]});
            skFitSpline(sketch, "E246", {"points": [v(-65.26, -9.46) * mm, v(-65.3, -9.66) * mm, v(-65.33, -9.86) * mm, v(-65.38, -10.04) * mm]});
            skFitSpline(sketch, "E247", {"points": [v(-65.38, -10.04) * mm, v(-65.44, -10.23) * mm, v(-65.48, -10.36) * mm, v(-65.51, -10.42) * mm]});
            skFitSpline(sketch, "E248", {"points": [v(-61.65, -8.94) * mm, v(-61.41, -7.48) * mm, v(-61.18, -6) * mm, v(-60.96, -4.51) * mm]});
            skFitSpline(sketch, "E249", {"points": [v(-53.92, 3.57) * mm, v(-52.36, 5.99) * mm, v(-51.58, 7.5) * mm, v(-51.58, 8.12) * mm]});
            skFitSpline(sketch, "E250", {"points": [v(-51.58, 8.12) * mm, v(-51.58, 9.11) * mm, v(-52, 9.6) * mm, v(-52.85, 9.6) * mm]});
            skFitSpline(sketch, "E251", {"points": [v(-52.85, 9.6) * mm, v(-53.5, 9.6) * mm, v(-54.35, 9.26) * mm, v(-55.42, 8.57) * mm]});
            skFitSpline(sketch, "E252", {"points": [v(-55.42, 8.57) * mm, v(-56.49, 7.87) * mm, v(-57.5, 6.92) * mm, v(-58.44, 5.7) * mm]});
            skFitSpline(sketch, "E253", {"points": [v(-60.27, 3.36) * mm, v(-60.88, 3.08) * mm, v(-61.19, 2.64) * mm, v(-61.19, 2.03) * mm]});
            skFitSpline(sketch, "E254", {"points": [v(-61.19, 2.03) * mm, v(-61.19, 1.93) * mm, v(-61.1, 1.8) * mm, v(-60.94, 1.63) * mm]});
            skFitSpline(sketch, "E255", {"points": [v(-60.94, 1.63) * mm, v(-60.66, 1.63) * mm, v(-60.24, 1.83) * mm, v(-59.66, 2.24) * mm]});
            skFitSpline(sketch, "E256", {"points": [v(-58.44, 3.3) * mm, v(-57.26, 4.53) * mm, v(-56.43, 5.13) * mm, v(-55.95, 5.13) * mm]});
            skFitSpline(sketch, "E257", {"points": [v(-55.95, 5.13) * mm, v(-55.72, 5.13) * mm, v(-55.6, 4.97) * mm, v(-55.6, 4.63) * mm]});
            skFitSpline(sketch, "E258", {"points": [v(-55.6, 4.63) * mm, v(-55.6, 4.19) * mm, v(-55.74, 3.54) * mm, v(-56.03, 2.7) * mm]});
            skFitSpline(sketch, "E259", {"points": [v(-56.03, 2.7) * mm, v(-56.32, 1.85) * mm, v(-56.5, 1.24) * mm, v(-56.56, 0.86) * mm]});
            skFitSpline(sketch, "E260", {"points": [v(-56.56, 0.86) * mm, v(-56.63, 0.5) * mm, v(-56.68, 0.19) * mm, v(-56.71, -0.05) * mm]});
            skFitSpline(sketch, "E261", {"points": [v(-56.71, -0.05) * mm, v(-56.4, -0.05) * mm, v(-55.48, 1.16) * mm, v(-53.92, 3.57) * mm]});
            skFitSpline(sketch, "E262", {"points": [v(-37.04, 7.08) * mm, v(-36.77, 7.22) * mm, v(-36.54, 7.45) * mm, v(-36.35, 7.78) * mm]});
            skFitSpline(sketch, "E263", {"points": [v(-36.35, 7.78) * mm, v(-36.17, 8.11) * mm, v(-36.07, 8.42) * mm, v(-36.07, 8.7) * mm]});
            skFitSpline(sketch, "E264", {"points": [v(-36.07, 8.7) * mm, v(-36.07, 9.2) * mm, v(-36.58, 9.47) * mm, v(-37.6, 9.47) * mm]});
            skFitSpline(sketch, "E265", {"points": [v(-41.46, 9.11) * mm, v(-42.38, 9.11) * mm, v(-43.24, 8.9) * mm, v(-44.06, 8.48) * mm]});
            skFitSpline(sketch, "E266", {"points": [v(-44.06, 8.48) * mm, v(-44.87, 8.05) * mm, v(-45.77, 7.3) * mm, v(-46.75, 6.24) * mm]});
            skFitSpline(sketch, "E267", {"points": [v(-46.75, 6.24) * mm, v(-47.73, 5.17) * mm, v(-48.5, 3.92) * mm, v(-49.04, 2.48) * mm]});
            skFitSpline(sketch, "E268", {"points": [v(-49.04, 2.48) * mm, v(-49.58, 1.04) * mm, v(-49.97, -0.14) * mm, v(-50.2, -1.06) * mm]});
            skFitSpline(sketch, "E269", {"points": [v(-50.2, -1.06) * mm, v(-50.44, -1.97) * mm, v(-50.62, -2.8) * mm, v(-50.74, -3.55) * mm]});
            skFitSpline(sketch, "E270", {"points": [v(-50.74, -3.55) * mm, v(-50.86, -4.3) * mm, v(-50.94, -4.91) * mm, v(-50.97, -5.4) * mm]});
            skFitSpline(sketch, "E271", {"points": [v(-50.97, -5.4) * mm, v(-51, -5.9) * mm, v(-51.02, -6.26) * mm, v(-51.02, -6.5) * mm]});
            skFitSpline(sketch, "E272", {"points": [v(-51.02, -6.5) * mm, v(-51.02, -9.17) * mm, v(-50.28, -10.51) * mm, v(-48.78, -10.51) * mm]});
            skFitSpline(sketch, "E273", {"points": [v(-48.78, -10.51) * mm, v(-47.4, -10.51) * mm, v(-45.46, -9.22) * mm, v(-42.99, -6.63) * mm]});
            skFitSpline(sketch, "E274", {"points": [v(-41.26, -4.74) * mm, v(-40.72, -4.2) * mm, v(-40.28, -3.63) * mm, v(-39.94, -3.05) * mm]});
            skFitSpline(sketch, "E275", {"points": [v(-39.94, -3.05) * mm, v(-39.6, -2.47) * mm, v(-39.43, -1.9) * mm, v(-39.43, -1.31) * mm]});
            skFitSpline(sketch, "E276", {"points": [v(-39.43, -1.31) * mm, v(-39.43, -1.14) * mm, v(-39.5, -0.94) * mm, v(-39.63, -0.7) * mm]});
            skFitSpline(sketch, "E277", {"points": [v(-40.8, -2.13) * mm, v(-41.51, -3.13) * mm, v(-42.36, -4.14) * mm, v(-43.34, -5.19) * mm]});
            skFitSpline(sketch, "E278", {"points": [v(-43.34, -5.19) * mm, v(-44.33, -6.23) * mm, v(-45.17, -6.75) * mm, v(-45.88, -6.75) * mm]});
            skFitSpline(sketch, "E279", {"points": [v(-45.88, -6.75) * mm, v(-46.73, -6.75) * mm, v(-47.16, -5.85) * mm, v(-47.16, -4.05) * mm]});
            skFitSpline(sketch, "E280", {"points": [v(-47.16, -4.05) * mm, v(-47.16, -2.8) * mm, v(-46.98, -1.25) * mm, v(-46.62, 0.6) * mm]});
            skFitSpline(sketch, "E281", {"points": [v(-46.62, 0.6) * mm, v(-46.27, 2.44) * mm, v(-45.86, 3.8) * mm, v(-45.4, 4.69) * mm]});
            skFitSpline(sketch, "E282", {"points": [v(-45.4, 4.69) * mm, v(-44.94, 5.57) * mm, v(-44.45, 6.16) * mm, v(-43.93, 6.44) * mm]});
            skFitSpline(sketch, "E283", {"points": [v(-43.93, 6.44) * mm, v(-43.4, 6.73) * mm, v(-42.8, 6.88) * mm, v(-42.12, 6.88) * mm]});
            skFitSpline(sketch, "E284", {"points": [v(-35.78, 7.58) * mm, v(-35.78, 8.76) * mm, v(-36.15, 9.36) * mm, v(-36.9, 9.36) * mm]});
            skFitSpline(sketch, "E285", {"points": [v(-36.9, 9.36) * mm, v(-37.3, 9.36) * mm, v(-37.79, 9.12) * mm, v(-38.36, 8.64) * mm]});
            skFitSpline(sketch, "E286", {"points": [v(-38.36, 8.64) * mm, v(-38.87, 8.13) * mm, v(-39.28, 7.48) * mm, v(-39.6, 6.68) * mm]});
            skFitSpline(sketch, "E287", {"points": [v(-39.6, 6.68) * mm, v(-39.92, 5.89) * mm, v(-40.15, 5.2) * mm, v(-40.28, 4.6) * mm]});
            skFitSpline(sketch, "E288", {"points": [v(-40.28, 4.6) * mm, v(-40.42, 4) * mm, v(-40.52, 3.29) * mm, v(-40.59, 2.44) * mm]});
            skFitSpline(sketch, "E289", {"points": [v(-41.82, -8.6) * mm, v(-41.82, -9.85) * mm, v(-41.53, -10.47) * mm, v(-40.95, -10.47) * mm]});
            skFitSpline(sketch, "E290", {"points": [v(-40.95, -10.47) * mm, v(-40.41, -10.47) * mm, v(-39.67, -10.1) * mm, v(-38.72, -9.36) * mm]});
            skFitSpline(sketch, "E291", {"points": [v(-38.72, -9.36) * mm, v(-37.77, -8.71) * mm, v(-36.22, -7.44) * mm, v(-34.09, -5.54) * mm]});
            skFitSpline(sketch, "E292", {"points": [v(-34.09, -5.54) * mm, v(-33.95, -5.37) * mm, v(-33.85, -5.24) * mm, v(-33.78, -5.13) * mm]});
            skFitSpline(sketch, "E293", {"points": [v(-33.78, -5.13) * mm, v(-33.72, -5.03) * mm, v(-33.67, -4.93) * mm, v(-33.63, -4.83) * mm]});
            skFitSpline(sketch, "E294", {"points": [v(-33.63, -4.83) * mm, v(-33.63, -4.76) * mm, v(-33.72, -4.68) * mm, v(-33.89, -4.58) * mm]});
            skFitSpline(sketch, "E295", {"points": [v(-33.89, -4.58) * mm, v(-34.12, -4.58) * mm, v(-34.42, -4.7) * mm, v(-34.78, -4.93) * mm]});
            skFitSpline(sketch, "E296", {"points": [v(-34.78, -4.93) * mm, v(-35.13, -5.17) * mm, v(-35.46, -5.4) * mm, v(-35.77, -5.64) * mm]});
            skFitSpline(sketch, "E297", {"points": [v(-35.77, -5.64) * mm, v(-36.07, -5.88) * mm, v(-36.34, -6.12) * mm, v(-36.58, -6.36) * mm]});
            skFitSpline(sketch, "E298", {"points": [v(-37.65, -7.12) * mm, v(-37.68, -7.09) * mm, v(-37.72, -7.03) * mm, v(-37.77, -6.94) * mm]});
            skFitSpline(sketch, "E299", {"points": [v(-37.77, -6.94) * mm, v(-37.83, -6.86) * mm, v(-37.85, -6.71) * mm, v(-37.85, -6.5) * mm]});
            skFitSpline(sketch, "E300", {"points": [v(-19.33, 7.12) * mm, v(-19.07, 7.3) * mm, v(-18.87, 7.5) * mm, v(-18.74, 7.75) * mm]});
            skFitSpline(sketch, "E301", {"points": [v(-18.33, 8.63) * mm, v(-18.33, 9.11) * mm, v(-18.84, 9.36) * mm, v(-19.85, 9.65) * mm]});
            skFitSpline(sketch, "E302", {"points": [v(-24.23, 9) * mm, v(-25.99, 8.83) * mm, v(-27.52, 8.2) * mm, v(-28.83, 7.11) * mm]});
            skFitSpline(sketch, "E303", {"points": [v(-28.83, 7.11) * mm, v(-30.13, 6.02) * mm, v(-31.2, 4.65) * mm, v(-32.06, 2.98) * mm]});
            skFitSpline(sketch, "E304", {"points": [v(-32.06, 2.98) * mm, v(-32.9, 1.32) * mm, v(-33.46, -0.38) * mm, v(-33.73, -2.11) * mm]});
            skFitSpline(sketch, "E305", {"points": [v(-33.73, -2.11) * mm, v(-34, -3.85) * mm, v(-34.14, -5.33) * mm, v(-34.14, -6.55) * mm]});
            skFitSpline(sketch, "E306", {"points": [v(-34.14, -6.55) * mm, v(-34.14, -9.3) * mm, v(-33.48, -10.68) * mm, v(-32.16, -10.68) * mm]});
            skFitSpline(sketch, "E307", {"points": [v(-32.16, -10.68) * mm, v(-31.04, -10.68) * mm, v(-29.4, -9.49) * mm, v(-27.23, -7.1) * mm]});
            skFitSpline(sketch, "E308", {"points": [v(-25.1, -4.86) * mm, v(-24.41, -4.14) * mm, v(-23.9, -3.6) * mm, v(-23.57, -3.22) * mm]});
            skFitSpline(sketch, "E309", {"points": [v(-23.57, -3.22) * mm, v(-23.23, -2.85) * mm, v(-22.88, -2.4) * mm, v(-22.52, -1.87) * mm]});
            skFitSpline(sketch, "E310", {"points": [v(-22.52, -1.87) * mm, v(-22.17, -1.34) * mm, v(-21.99, -0.79) * mm, v(-21.99, -0.2) * mm]});
            skFitSpline(sketch, "E311", {"points": [v(-21.99, -0.2) * mm, v(-21.99, 0.27) * mm, v(-22.1, 0.5) * mm, v(-22.3, 0.5) * mm]});
            skFitSpline(sketch, "E312", {"points": [v(-22.3, 0.5) * mm, v(-22.5, 0.5) * mm, v(-22.75, 0.32) * mm, v(-23.06, -0.05) * mm]});
            skFitSpline(sketch, "E313", {"points": [v(-26.87, -5.02) * mm, v(-28.2, -6.42) * mm, v(-29.18, -7.12) * mm, v(-29.82, -7.12) * mm]});
            skFitSpline(sketch, "E314", {"points": [v(-29.82, -7.12) * mm, v(-30.4, -7.12) * mm, v(-30.68, -6.58) * mm, v(-30.68, -5.5) * mm]});
            skFitSpline(sketch, "E315", {"points": [v(-29.46, 1.1) * mm, v(-29.16, 2.66) * mm, v(-28.76, 3.88) * mm, v(-28.27, 4.77) * mm]});
            skFitSpline(sketch, "E316", {"points": [v(-28.27, 4.77) * mm, v(-27.78, 5.66) * mm, v(-27.24, 6.24) * mm, v(-26.67, 6.5) * mm]});
            skFitSpline(sketch, "E317", {"points": [v(-26.67, 6.5) * mm, v(-26.1, 6.78) * mm, v(-25.45, 6.91) * mm, v(-24.73, 6.88) * mm]});
            skFitSpline(sketch, "E318", {"points": [v(-20.46, 8.73) * mm, v(-20.77, 8.73) * mm, v(-21.2, 8.73) * mm, v(-21.79, 8.73) * mm]});
            skFitSpline(sketch, "E319", {"points": [v(-21.79, 8.73) * mm, v(-22.23, 8.73) * mm, v(-22.45, 8.6) * mm, v(-22.45, 8.37) * mm]});
            skFitSpline(sketch, "E320", {"points": [v(-25.1, -14.82) * mm, v(-25.1, -15.73) * mm, v(-25.14, -16.5) * mm, v(-25.24, -17.13) * mm]});
            skFitSpline(sketch, "E321", {"points": [v(-25.24, -17.13) * mm, v(-25.34, -17.76) * mm, v(-25.48, -18.4) * mm, v(-25.65, -19.04) * mm]});
            skFitSpline(sketch, "E322", {"points": [v(-25.65, -19.04) * mm, v(-25.92, -19.81) * mm, v(-26.36, -20.4) * mm, v(-26.97, -20.76) * mm]});
            skFitSpline(sketch, "E323", {"points": [v(-26.97, -20.76) * mm, v(-27.65, -21.27) * mm, v(-28.63, -21.53) * mm, v(-29.92, -21.53) * mm]});
            skFitSpline(sketch, "E324", {"points": [v(-29.92, -21.53) * mm, v(-31.2, -21.53) * mm, v(-32.34, -21.15) * mm, v(-33.3, -20.38) * mm]});
            skFitSpline(sketch, "E325", {"points": [v(-33.3, -20.38) * mm, v(-34.27, -19.62) * mm, v(-34.75, -18.73) * mm, v(-34.75, -17.71) * mm]});
            skFitSpline(sketch, "E326", {"points": [v(-34.75, -17.71) * mm, v(-34.75, -17.3) * mm, v(-34.6, -16.76) * mm, v(-34.27, -16.06) * mm]});
            skFitSpline(sketch, "E327", {"points": [v(-34.27, -16.06) * mm, v(-33.95, -15.37) * mm, v(-33.42, -14.73) * mm, v(-32.7, -14.15) * mm]});
            skFitSpline(sketch, "E328", {"points": [v(-32.7, -14.15) * mm, v(-31.96, -13.58) * mm, v(-31.43, -13.18) * mm, v(-31.1, -12.96) * mm]});
            skFitSpline(sketch, "E329", {"points": [v(-31.1, -12.96) * mm, v(-30.75, -12.74) * mm, v(-30.31, -12.5) * mm, v(-29.77, -12.22) * mm]});
            skFitSpline(sketch, "E330", {"points": [v(-27.07, -11.15) * mm, v(-26.63, -10.98) * mm, v(-26.31, -10.85) * mm, v(-26.1, -10.75) * mm]});
            skFitSpline(sketch, "E331", {"points": [v(-26.1, -10.75) * mm, v(-25.9, -10.65) * mm, v(-25.73, -10.53) * mm, v(-25.6, -10.4) * mm]});
            skFitSpline(sketch, "E332", {"points": [v(-25.7, -10.24) * mm, v(-26.28, -10.24) * mm, v(-27.28, -10.56) * mm, v(-28.7, -11.2) * mm]});
            skFitSpline(sketch, "E333", {"points": [v(-28.7, -11.2) * mm, v(-30.12, -11.85) * mm, v(-31.52, -12.64) * mm, v(-32.9, -13.6) * mm]});
            skFitSpline(sketch, "E334", {"points": [v(-32.9, -13.6) * mm, v(-34.27, -14.54) * mm, v(-35.22, -15.46) * mm, v(-35.74, -16.34) * mm]});
            skFitSpline(sketch, "E335", {"points": [v(-35.74, -16.34) * mm, v(-36.27, -17.22) * mm, v(-36.53, -18.3) * mm, v(-36.53, -19.6) * mm]});
            skFitSpline(sketch, "E336", {"points": [v(-36.53, -19.6) * mm, v(-36.53, -20.88) * mm, v(-36.15, -22) * mm, v(-35.39, -22.95) * mm]});
            skFitSpline(sketch, "E337", {"points": [v(-35.39, -22.95) * mm, v(-34.62, -23.9) * mm, v(-33.55, -24.37) * mm, v(-32.16, -24.37) * mm]});
            skFitSpline(sketch, "E338", {"points": [v(-32.16, -24.37) * mm, v(-30.4, -24.37) * mm, v(-28.52, -23.65) * mm, v(-26.54, -22.19) * mm]});
            skFitSpline(sketch, "E339", {"points": [v(-26.54, -22.19) * mm, v(-24.56, -20.73) * mm, v(-23.22, -18.92) * mm, v(-22.52, -16.77) * mm]});
            skFitSpline(sketch, "E340", {"points": [v(-22.52, -16.77) * mm, v(-21.83, -14.62) * mm, v(-21.3, -11.88) * mm, v(-20.92, -8.56) * mm]});
            skFitSpline(sketch, "E341", {"points": [v(-19.96, 0.74) * mm, v(-19.65, 3.7) * mm, v(-19.24, 6.13) * mm, v(-18.74, 8.06) * mm]});
            skFitSpline(sketch, "E342", {"points": [v(-18.74, 8.06) * mm, v(-18.74, 8.5) * mm, v(-19.31, 8.73) * mm, v(-20.46, 8.73) * mm]});
            skFitSpline(sketch, "E343", {"points": [v(-4.65, 7.08) * mm, v(-4.38, 7.22) * mm, v(-4.15, 7.45) * mm, v(-3.97, 7.78) * mm]});
            skFitSpline(sketch, "E344", {"points": [v(-3.97, 7.78) * mm, v(-3.78, 8.11) * mm, v(-3.69, 8.42) * mm, v(-3.69, 8.7) * mm]});
            skFitSpline(sketch, "E345", {"points": [v(-3.69, 8.7) * mm, v(-3.69, 9.2) * mm, v(-4.2, 9.47) * mm, v(-5.21, 9.47) * mm]});
            skFitSpline(sketch, "E346", {"points": [v(-9.08, 9.11) * mm, v(-10, 9.11) * mm, v(-10.86, 8.9) * mm, v(-11.67, 8.48) * mm]});
            skFitSpline(sketch, "E347", {"points": [v(-11.67, 8.48) * mm, v(-12.48, 8.05) * mm, v(-13.38, 7.3) * mm, v(-14.36, 6.24) * mm]});
            skFitSpline(sketch, "E348", {"points": [v(-14.36, 6.24) * mm, v(-15.35, 5.17) * mm, v(-16.1, 3.92) * mm, v(-16.65, 2.48) * mm]});
            skFitSpline(sketch, "E349", {"points": [v(-16.65, 2.48) * mm, v(-17.2, 1.04) * mm, v(-17.58, -0.14) * mm, v(-17.82, -1.06) * mm]});
            skFitSpline(sketch, "E350", {"points": [v(-17.82, -1.06) * mm, v(-18.06, -1.97) * mm, v(-18.24, -2.8) * mm, v(-18.35, -3.55) * mm]});
            skFitSpline(sketch, "E351", {"points": [v(-18.35, -3.55) * mm, v(-18.47, -4.3) * mm, v(-18.55, -4.91) * mm, v(-18.58, -5.4) * mm]});
            skFitSpline(sketch, "E352", {"points": [v(-18.58, -5.4) * mm, v(-18.62, -5.9) * mm, v(-18.63, -6.26) * mm, v(-18.63, -6.5) * mm]});
            skFitSpline(sketch, "E353", {"points": [v(-18.63, -6.5) * mm, v(-18.63, -9.17) * mm, v(-17.89, -10.51) * mm, v(-16.4, -10.51) * mm]});
            skFitSpline(sketch, "E354", {"points": [v(-16.4, -10.51) * mm, v(-15, -10.51) * mm, v(-13.07, -9.22) * mm, v(-10.6, -6.63) * mm]});
            skFitSpline(sketch, "E355", {"points": [v(-8.87, -4.74) * mm, v(-8.33, -4.2) * mm, v(-7.89, -3.63) * mm, v(-7.55, -3.05) * mm]});
            skFitSpline(sketch, "E356", {"points": [v(-7.55, -3.05) * mm, v(-7.21, -2.47) * mm, v(-7.04, -1.9) * mm, v(-7.04, -1.31) * mm]});
            skFitSpline(sketch, "E357", {"points": [v(-7.04, -1.31) * mm, v(-7.04, -1.14) * mm, v(-7.1, -0.94) * mm, v(-7.24, -0.7) * mm]});
            skFitSpline(sketch, "E358", {"points": [v(-8.41, -2.13) * mm, v(-9.13, -3.13) * mm, v(-9.97, -4.14) * mm, v(-10.96, -5.19) * mm]});
            skFitSpline(sketch, "E359", {"points": [v(-10.96, -5.19) * mm, v(-11.94, -6.23) * mm, v(-12.79, -6.75) * mm, v(-13.5, -6.75) * mm]});
            skFitSpline(sketch, "E360", {"points": [v(-13.5, -6.75) * mm, v(-14.35, -6.75) * mm, v(-14.77, -5.85) * mm, v(-14.77, -4.05) * mm]});
            skFitSpline(sketch, "E361", {"points": [v(-14.77, -4.05) * mm, v(-14.77, -2.8) * mm, v(-14.6, -1.25) * mm, v(-14.24, 0.6) * mm]});
            skFitSpline(sketch, "E362", {"points": [v(-14.24, 0.6) * mm, v(-13.88, 2.44) * mm, v(-13.47, 3.8) * mm, v(-13.02, 4.69) * mm]});
            skFitSpline(sketch, "E363", {"points": [v(-13.02, 4.69) * mm, v(-12.56, 5.57) * mm, v(-12.07, 6.16) * mm, v(-11.54, 6.44) * mm]});
            skFitSpline(sketch, "E364", {"points": [v(-11.54, 6.44) * mm, v(-11.02, 6.73) * mm, v(-10.41, 6.88) * mm, v(-9.74, 6.88) * mm]});
            skFitSpline(sketch, "E365", {"points": [v(-3.4, 7.58) * mm, v(-3.4, 8.76) * mm, v(-3.76, 9.36) * mm, v(-4.5, 9.36) * mm]});
            skFitSpline(sketch, "E366", {"points": [v(-4.5, 9.36) * mm, v(-4.91, 9.36) * mm, v(-5.4, 9.12) * mm, v(-5.97, 8.64) * mm]});
            skFitSpline(sketch, "E367", {"points": [v(-5.97, 8.64) * mm, v(-6.48, 8.13) * mm, v(-6.9, 7.48) * mm, v(-7.21, 6.68) * mm]});
            skFitSpline(sketch, "E368", {"points": [v(-7.21, 6.68) * mm, v(-7.53, 5.89) * mm, v(-7.76, 5.2) * mm, v(-7.9, 4.6) * mm]});
            skFitSpline(sketch, "E369", {"points": [v(-7.9, 4.6) * mm, v(-8.03, 4) * mm, v(-8.13, 3.29) * mm, v(-8.2, 2.44) * mm]});
            skFitSpline(sketch, "E370", {"points": [v(-9.43, -8.6) * mm, v(-9.43, -9.85) * mm, v(-9.14, -10.47) * mm, v(-8.57, -10.47) * mm]});
            skFitSpline(sketch, "E371", {"points": [v(-8.57, -10.47) * mm, v(-8.03, -10.47) * mm, v(-7.28, -10.1) * mm, v(-6.33, -9.36) * mm]});
            skFitSpline(sketch, "E372", {"points": [v(-6.33, -9.36) * mm, v(-5.38, -8.71) * mm, v(-3.84, -7.44) * mm, v(-1.7, -5.54) * mm]});
            skFitSpline(sketch, "E373", {"points": [v(-1.7, -5.54) * mm, v(-1.57, -5.37) * mm, v(-1.47, -5.24) * mm, v(-1.4, -5.13) * mm]});
            skFitSpline(sketch, "E374", {"points": [v(-1.4, -5.13) * mm, v(-1.33, -5.03) * mm, v(-1.28, -4.93) * mm, v(-1.24, -4.83) * mm]});
            skFitSpline(sketch, "E375", {"points": [v(-1.24, -4.83) * mm, v(-1.24, -4.76) * mm, v(-1.33, -4.68) * mm, v(-1.5, -4.58) * mm]});
            skFitSpline(sketch, "E376", {"points": [v(-1.5, -4.58) * mm, v(-1.74, -4.58) * mm, v(-2.03, -4.7) * mm, v(-2.39, -4.93) * mm]});
            skFitSpline(sketch, "E377", {"points": [v(-2.39, -4.93) * mm, v(-2.74, -5.17) * mm, v(-3.08, -5.4) * mm, v(-3.38, -5.64) * mm]});
            skFitSpline(sketch, "E378", {"points": [v(-3.38, -5.64) * mm, v(-3.69, -5.88) * mm, v(-3.96, -6.12) * mm, v(-4.2, -6.36) * mm]});
            skFitSpline(sketch, "E379", {"points": [v(-5.26, -7.12) * mm, v(-5.3, -7.09) * mm, v(-5.34, -7.03) * mm, v(-5.39, -6.94) * mm]});
            skFitSpline(sketch, "E380", {"points": [v(-5.39, -6.94) * mm, v(-5.44, -6.86) * mm, v(-5.47, -6.71) * mm, v(-5.47, -6.5) * mm]});
            skFitSpline(sketch, "E381", {"points": [v(0.15, 3.81) * mm, v(0.81, 4.6) * mm, v(1.4, 4.98) * mm, v(1.9, 4.98) * mm]});
            skFitSpline(sketch, "E382", {"points": [v(1.9, 4.98) * mm, v(2.31, 4.98) * mm, v(2.52, 4.42) * mm, v(2.52, 3.3) * mm]});
            skFitSpline(sketch, "E383", {"points": [v(0.12, -13.32) * mm, v(-0.69, -17.96) * mm, v(-1.1, -21.07) * mm, v(-1.1, -22.63) * mm]});
            skFitSpline(sketch, "E384", {"points": [v(-1.1, -22.63) * mm, v(-1.1, -23.91) * mm, v(-0.79, -24.56) * mm, v(-0.18, -24.56) * mm]});
            skFitSpline(sketch, "E385", {"points": [v(1.5, -23.95) * mm, v(2.04, -23.68) * mm, v(2.47, -23.47) * mm, v(2.8, -23.34) * mm]});
            skFitSpline(sketch, "E386", {"points": [v(2.8, -23.34) * mm, v(3.12, -23.2) * mm, v(3.5, -23.05) * mm, v(3.94, -22.88) * mm]});
            skFitSpline(sketch, "E387", {"points": [v(3.94, -22.88) * mm, v(4.38, -22.71) * mm, v(5.04, -22.63) * mm, v(5.92, -22.63) * mm]});
            skFitSpline(sketch, "E388", {"points": [v(5.92, -22.63) * mm, v(6.57, -22.63) * mm, v(6.9, -22.17) * mm, v(6.9, -21.25) * mm]});
            skFitSpline(sketch, "E389", {"points": [v(6.9, -21.25) * mm, v(6.9, -20.64) * mm, v(6.6, -20.34) * mm, v(6.03, -20.34) * mm]});
            skFitSpline(sketch, "E390", {"points": [v(6.03, -20.34) * mm, v(4.97, -20.98) * mm, v(4.31, -21.3) * mm, v(4.04, -21.3) * mm]});
            skFitSpline(sketch, "E391", {"points": [v(4.04, -21.3) * mm, v(3.67, -21.3) * mm, v(3.48, -20.88) * mm, v(3.48, -20.03) * mm]});
            skFitSpline(sketch, "E392", {"points": [v(6.58, 6.97) * mm, v(6.58, 8.46) * mm, v(6.26, 9.2) * mm, v(5.62, 9.2) * mm]});
            skFitSpline(sketch, "E393", {"points": [v(5.62, 9.2) * mm, v(4.7, 9.2) * mm, v(3.28, 8.28) * mm, v(1.35, 6.43) * mm]});
            skFitSpline(sketch, "E394", {"points": [v(1.35, 6.43) * mm, v(-0.58, 4.58) * mm, v(-1.55, 3.47) * mm, v(-1.55, 3.1) * mm]});
            skFitSpline(sketch, "E395", {"points": [v(-1.55, 3.1) * mm, v(-1.55, 2.8) * mm, v(-1.43, 2.64) * mm, v(-1.2, 2.64) * mm]});
            skFitSpline(sketch, "E396", {"points": [v(-1.2, 2.64) * mm, v(-0.96, 2.64) * mm, v(-0.5, 3.03) * mm, v(0.15, 3.81) * mm]});
            skFitSpline(sketch, "E397", {"points": [v(4.8, -8.5) * mm, v(4.53, -8.27) * mm, v(4.25, -8.15) * mm, v(3.94, -8.15) * mm]});
            skFitSpline(sketch, "E398", {"points": [v(3.94, -8.15) * mm, v(3.74, -8.19) * mm, v(3.6, -8.27) * mm, v(3.53, -8.41) * mm]});
            skFitSpline(sketch, "E399", {"points": [v(3.53, -8.41) * mm, v(3.47, -8.56) * mm, v(3.43, -8.74) * mm, v(3.43, -8.96) * mm]});
            skFitSpline(sketch, "E400", {"points": [v(3.28, -9.48) * mm, v(2.97, -10.02) * mm, v(2.82, -10.43) * mm, v(2.82, -10.68) * mm]});
            skFitSpline(sketch, "E401", {"points": [v(8.28, -10.7) * mm, v(10.95, -10.7) * mm, v(12.78, -9.46) * mm, v(13.75, -7) * mm]});
            skFitSpline(sketch, "E402", {"points": [v(13.75, -7) * mm, v(14.73, -4.53) * mm, v(15.39, -2.2) * mm, v(15.73, 0) * mm]});
            skFitSpline(sketch, "E403", {"points": [v(15.73, 0) * mm, v(16.07, 2.2) * mm, v(16.26, 3.58) * mm, v(16.3, 4.14) * mm]});
            skFitSpline(sketch, "E404", {"points": [v(16.3, 4.14) * mm, v(16.33, 4.7) * mm, v(16.35, 5.23) * mm, v(16.35, 5.74) * mm]});
            skFitSpline(sketch, "E405", {"points": [v(16.35, 5.74) * mm, v(16.35, 8.1) * mm, v(15.75, 9.29) * mm, v(14.57, 9.29) * mm]});
            skFitSpline(sketch, "E406", {"points": [v(14.57, 9.29) * mm, v(13.38, 9.29) * mm, v(11.52, 7.94) * mm, v(8.97, 5.25) * mm]});
            skFitSpline(sketch, "E407", {"points": [v(7.2, 3.56) * mm, v(6.31, 2.74) * mm, v(5.69, 2.1) * mm, v(5.31, 1.62) * mm]});
            skFitSpline(sketch, "E408", {"points": [v(5.31, 1.62) * mm, v(4.94, 1.14) * mm, v(4.75, 0.63) * mm, v(4.75, 0.09) * mm]});
            skFitSpline(sketch, "E409", {"points": [v(4.75, 0.09) * mm, v(4.75, -0.05) * mm, v(4.84, -0.2) * mm, v(5, -0.37) * mm]});
            skFitSpline(sketch, "E410", {"points": [v(5, -0.37) * mm, v(5.45, -0.37) * mm, v(6.5, 0.6) * mm, v(8.16, 2.57) * mm]});
            skFitSpline(sketch, "E411", {"points": [v(8.16, 2.57) * mm, v(9.59, 4.1) * mm, v(10.65, 4.86) * mm, v(11.36, 4.86) * mm]});
            skFitSpline(sketch, "E412", {"points": [v(11.36, 4.86) * mm, v(12.1, 4.86) * mm, v(12.48, 4.08) * mm, v(12.48, 2.52) * mm]});
            skFitSpline(sketch, "E413", {"points": [v(12.48, 2.52) * mm, v(12.48, 1.13) * mm, v(12.25, -0.65) * mm, v(11.8, -2.82) * mm]});
            skFitSpline(sketch, "E414", {"points": [v(11.8, -2.82) * mm, v(11.34, -4.98) * mm, v(10.76, -6.64) * mm, v(10.07, -7.77) * mm]});
            skFitSpline(sketch, "E415", {"points": [v(10.07, -7.77) * mm, v(9.37, -8.9) * mm, v(8.55, -9.48) * mm, v(7.6, -9.48) * mm]});
            skFitSpline(sketch, "E416", {"points": [v(7.6, -9.48) * mm, v(6.79, -9.48) * mm, v(5.86, -9.15) * mm, v(4.8, -8.5) * mm]});
            skFitSpline(sketch, "E417", {"points": [v(30.68, 7.08) * mm, v(30.96, 7.22) * mm, v(31.18, 7.45) * mm, v(31.37, 7.78) * mm]});
            skFitSpline(sketch, "E418", {"points": [v(31.37, 7.78) * mm, v(31.56, 8.11) * mm, v(31.65, 8.42) * mm, v(31.65, 8.7) * mm]});
            skFitSpline(sketch, "E419", {"points": [v(31.65, 8.7) * mm, v(31.65, 9.2) * mm, v(31.14, 9.47) * mm, v(30.13, 9.47) * mm]});
            skFitSpline(sketch, "E420", {"points": [v(26.26, 9.11) * mm, v(25.35, 9.11) * mm, v(24.48, 8.9) * mm, v(23.67, 8.48) * mm]});
            skFitSpline(sketch, "E421", {"points": [v(23.67, 8.48) * mm, v(22.85, 8.05) * mm, v(21.96, 7.3) * mm, v(20.97, 6.24) * mm]});
            skFitSpline(sketch, "E422", {"points": [v(20.97, 6.24) * mm, v(19.99, 5.17) * mm, v(19.23, 3.92) * mm, v(18.68, 2.48) * mm]});
            skFitSpline(sketch, "E423", {"points": [v(18.68, 2.48) * mm, v(18.14, 1.04) * mm, v(17.75, -0.14) * mm, v(17.52, -1.06) * mm]});
            skFitSpline(sketch, "E424", {"points": [v(17.52, -1.06) * mm, v(17.28, -1.97) * mm, v(17.1, -2.8) * mm, v(16.98, -3.55) * mm]});
            skFitSpline(sketch, "E425", {"points": [v(16.98, -3.55) * mm, v(16.86, -4.3) * mm, v(16.79, -4.91) * mm, v(16.75, -5.4) * mm]});
            skFitSpline(sketch, "E426", {"points": [v(16.75, -5.4) * mm, v(16.72, -5.9) * mm, v(16.7, -6.26) * mm, v(16.7, -6.5) * mm]});
            skFitSpline(sketch, "E427", {"points": [v(16.7, -6.5) * mm, v(16.7, -9.17) * mm, v(17.45, -10.51) * mm, v(18.94, -10.51) * mm]});
            skFitSpline(sketch, "E428", {"points": [v(18.94, -10.51) * mm, v(20.33, -10.51) * mm, v(22.26, -9.22) * mm, v(24.74, -6.63) * mm]});
            skFitSpline(sketch, "E429", {"points": [v(26.46, -4.74) * mm, v(27, -4.2) * mm, v(27.45, -3.63) * mm, v(27.79, -3.05) * mm]});
            skFitSpline(sketch, "E430", {"points": [v(27.79, -3.05) * mm, v(28.12, -2.47) * mm, v(28.3, -1.9) * mm, v(28.3, -1.31) * mm]});
            skFitSpline(sketch, "E431", {"points": [v(28.3, -1.31) * mm, v(28.3, -1.14) * mm, v(28.23, -0.94) * mm, v(28.1, -0.7) * mm]});
            skFitSpline(sketch, "E432", {"points": [v(26.92, -2.13) * mm, v(26.2, -3.13) * mm, v(25.36, -4.14) * mm, v(24.38, -5.19) * mm]});
            skFitSpline(sketch, "E433", {"points": [v(24.38, -5.19) * mm, v(23.4, -6.23) * mm, v(22.55, -6.75) * mm, v(21.84, -6.75) * mm]});
            skFitSpline(sketch, "E434", {"points": [v(21.84, -6.75) * mm, v(20.99, -6.75) * mm, v(20.57, -5.85) * mm, v(20.57, -4.05) * mm]});
            skFitSpline(sketch, "E435", {"points": [v(20.57, -4.05) * mm, v(20.57, -2.8) * mm, v(20.74, -1.25) * mm, v(21.1, 0.6) * mm]});
            skFitSpline(sketch, "E436", {"points": [v(21.1, 0.6) * mm, v(21.46, 2.44) * mm, v(21.86, 3.8) * mm, v(22.32, 4.69) * mm]});
            skFitSpline(sketch, "E437", {"points": [v(22.32, 4.69) * mm, v(22.78, 5.57) * mm, v(23.27, 6.16) * mm, v(23.8, 6.44) * mm]});
            skFitSpline(sketch, "E438", {"points": [v(23.8, 6.44) * mm, v(24.32, 6.73) * mm, v(24.92, 6.88) * mm, v(25.6, 6.88) * mm]});
            skFitSpline(sketch, "E439", {"points": [v(31.94, 7.58) * mm, v(31.94, 8.76) * mm, v(31.57, 9.36) * mm, v(30.83, 9.36) * mm]});
            skFitSpline(sketch, "E440", {"points": [v(30.83, 9.36) * mm, v(30.42, 9.36) * mm, v(29.93, 9.12) * mm, v(29.36, 8.64) * mm]});
            skFitSpline(sketch, "E441", {"points": [v(29.36, 8.64) * mm, v(28.85, 8.13) * mm, v(28.44, 7.48) * mm, v(28.12, 6.68) * mm]});
            skFitSpline(sketch, "E442", {"points": [v(28.12, 6.68) * mm, v(27.8, 5.89) * mm, v(27.57, 5.2) * mm, v(27.44, 4.6) * mm]});
            skFitSpline(sketch, "E443", {"points": [v(27.44, 4.6) * mm, v(27.3, 4) * mm, v(27.2, 3.29) * mm, v(27.14, 2.44) * mm]});
            skFitSpline(sketch, "E444", {"points": [v(25.9, -8.6) * mm, v(25.9, -9.85) * mm, v(26.2, -10.47) * mm, v(26.77, -10.47) * mm]});
            skFitSpline(sketch, "E445", {"points": [v(26.77, -10.47) * mm, v(27.31, -10.47) * mm, v(28.06, -10.1) * mm, v(29, -9.36) * mm]});
            skFitSpline(sketch, "E446", {"points": [v(29, -9.36) * mm, v(29.96, -8.71) * mm, v(31.5, -7.44) * mm, v(33.63, -5.54) * mm]});
            skFitSpline(sketch, "E447", {"points": [v(33.63, -5.54) * mm, v(33.77, -5.37) * mm, v(33.87, -5.24) * mm, v(33.94, -5.13) * mm]});
            skFitSpline(sketch, "E448", {"points": [v(33.94, -5.13) * mm, v(34, -5.03) * mm, v(34.06, -4.93) * mm, v(34.1, -4.83) * mm]});
            skFitSpline(sketch, "E449", {"points": [v(34.1, -4.83) * mm, v(34.1, -4.76) * mm, v(34, -4.68) * mm, v(33.84, -4.58) * mm]});
            skFitSpline(sketch, "E450", {"points": [v(33.84, -4.58) * mm, v(33.6, -4.58) * mm, v(33.3, -4.7) * mm, v(32.95, -4.93) * mm]});
            skFitSpline(sketch, "E451", {"points": [v(32.95, -4.93) * mm, v(32.6, -5.17) * mm, v(32.26, -5.4) * mm, v(31.95, -5.64) * mm]});
            skFitSpline(sketch, "E452", {"points": [v(31.95, -5.64) * mm, v(31.65, -5.88) * mm, v(31.38, -6.12) * mm, v(31.14, -6.36) * mm]});
            skFitSpline(sketch, "E453", {"points": [v(30.07, -7.12) * mm, v(30.04, -7.09) * mm, v(30, -7.03) * mm, v(29.95, -6.94) * mm]});
            skFitSpline(sketch, "E454", {"points": [v(29.95, -6.94) * mm, v(29.9, -6.86) * mm, v(29.87, -6.71) * mm, v(29.87, -6.5) * mm]});
            skFitSpline(sketch, "E455", {"points": [v(41.77, -5.06) * mm, v(41.02, -5.82) * mm, v(40.46, -6.2) * mm, v(40.09, -6.2) * mm]});
            skFitSpline(sketch, "E456", {"points": [v(40.09, -6.2) * mm, v(39.68, -6.2) * mm, v(39.48, -5.63) * mm, v(39.48, -4.47) * mm]});
            skFitSpline(sketch, "E457", {"points": [v(41.88, 12.05) * mm, v(42.89, 17.81) * mm, v(43.4, 21.35) * mm, v(43.4, 22.68) * mm]});
            skFitSpline(sketch, "E458", {"points": [v(43.4, 22.68) * mm, v(43.4, 23.73) * mm, v(43.16, 24.25) * mm, v(42.68, 24.25) * mm]});
            skFitSpline(sketch, "E459", {"points": [v(42.68, 24.25) * mm, v(42.34, 24.25) * mm, v(42, 24.13) * mm, v(41.67, 23.9) * mm]});
            skFitSpline(sketch, "E460", {"points": [v(39.12, 22.22) * mm, v(37.9, 21.37) * mm, v(36.92, 20.74) * mm, v(36.17, 20.31) * mm]});
            skFitSpline(sketch, "E461", {"points": [v(36.17, 20.31) * mm, v(35.43, 19.89) * mm, v(35.06, 19.5) * mm, v(35.06, 19.17) * mm]});
            skFitSpline(sketch, "E462", {"points": [v(35.06, 19.17) * mm, v(35.12, 18.9) * mm, v(35.26, 18.76) * mm, v(35.46, 18.76) * mm]});
            skFitSpline(sketch, "E463", {"points": [v(36.07, 18.97) * mm, v(37.36, 19.74) * mm, v(38.1, 20.13) * mm, v(38.3, 20.13) * mm]});
            skFitSpline(sketch, "E464", {"points": [v(38.3, 20.13) * mm, v(38.65, 20.13) * mm, v(38.82, 19.78) * mm, v(38.82, 19.07) * mm]});
            skFitSpline(sketch, "E465", {"points": [v(35.26, -8.8) * mm, v(35.26, -10.15) * mm, v(35.56, -10.83) * mm, v(36.17, -10.83) * mm]});
            skFitSpline(sketch, "E466", {"points": [v(36.17, -10.83) * mm, v(37.09, -10.83) * mm, v(38.56, -9.81) * mm, v(40.6, -7.78) * mm]});
            skFitSpline(sketch, "E467", {"points": [v(40.6, -7.78) * mm, v(42.63, -5.75) * mm, v(43.65, -4.58) * mm, v(43.65, -4.27) * mm]});
            skFitSpline(sketch, "E468", {"points": [v(43.65, -4.27) * mm, v(43.65, -4.03) * mm, v(43.51, -3.91) * mm, v(43.24, -3.91) * mm]});
            skFitSpline(sketch, "E469", {"points": [v(43.24, -3.91) * mm, v(43, -3.91) * mm, v(42.51, -4.3) * mm, v(41.77, -5.06) * mm]});
            skFitSpline(sketch, "E470", {"points": [v(50.51, 8.6) * mm, v(48.92, 8.05) * mm, v(47.77, 7.42) * mm, v(47.05, 6.7) * mm]});
            skFitSpline(sketch, "E471", {"points": [v(47.05, 6.7) * mm, v(46.34, 5.97) * mm, v(45.65, 4.44) * mm, v(44.97, 2.1) * mm]});
            skFitSpline(sketch, "E472", {"points": [v(44.97, 2.1) * mm, v(44.3, -0.23) * mm, v(43.95, -2.16) * mm, v(43.95, -3.68) * mm]});
            skFitSpline(sketch, "E473", {"points": [v(43.95, -3.68) * mm, v(43.95, -5.57) * mm, v(44.34, -7.2) * mm, v(45.12, -8.55) * mm]});
            skFitSpline(sketch, "E474", {"points": [v(45.12, -8.55) * mm, v(45.9, -9.9) * mm, v(46.99, -10.58) * mm, v(48.38, -10.58) * mm]});
            skFitSpline(sketch, "E475", {"points": [v(48.38, -10.58) * mm, v(49.8, -10.58) * mm, v(51.17, -10.12) * mm, v(52.5, -9.2) * mm]});
            skFitSpline(sketch, "E476", {"points": [v(55.09, -7.53) * mm, v(55.56, -7.23) * mm, v(55.97, -6.93) * mm, v(56.3, -6.65) * mm]});
            skFitSpline(sketch, "E477", {"points": [v(56.3, -6.65) * mm, v(56.65, -6.36) * mm, v(56.99, -6.05) * mm, v(57.33, -5.7) * mm]});
            skFitSpline(sketch, "E478", {"points": [v(57.33, -5.7) * mm, v(57.66, -5.37) * mm, v(57.92, -4.8) * mm, v(58.09, -3.98) * mm]});
            skFitSpline(sketch, "E479", {"points": [v(59.46, 3.12) * mm, v(59.46, 4.64) * mm, v(58.83, 6.1) * mm, v(57.55, 7.5) * mm]});
            skFitSpline(sketch, "E480", {"points": [v(57.55, 7.5) * mm, v(56.28, 8.9) * mm, v(55.2, 9.6) * mm, v(54.28, 9.6) * mm]});
            skFitSpline(sketch, "E481", {"points": [v(49.55, 5.19) * mm, v(49.78, 5.86) * mm, v(50.04, 6.39) * mm, v(50.3, 6.76) * mm]});
            skFitSpline(sketch, "E482", {"points": [v(50.3, 6.76) * mm, v(50.65, 7.1) * mm, v(50.9, 7.32) * mm, v(51.05, 7.42) * mm]});
            skFitSpline(sketch, "E483", {"points": [v(51.05, 7.42) * mm, v(51.2, 7.52) * mm, v(51.39, 7.65) * mm, v(51.6, 7.8) * mm]});
            skFitSpline(sketch, "E484", {"points": [v(51.6, 7.8) * mm, v(51.83, 7.96) * mm, v(52.09, 8.03) * mm, v(52.4, 8.03) * mm]});
            skFitSpline(sketch, "E485", {"points": [v(52.4, 8.03) * mm, v(52.97, 8.03) * mm, v(53.49, 7.75) * mm, v(53.95, 7.2) * mm]});
            skFitSpline(sketch, "E486", {"points": [v(53.95, 7.2) * mm, v(54.4, 6.63) * mm, v(54.68, 6.03) * mm, v(54.78, 5.39) * mm]});
            skFitSpline(sketch, "E487", {"points": [v(54.78, 5.39) * mm, v(55.06, 4.2) * mm, v(55.2, 3.03) * mm, v(55.2, 1.88) * mm]});
            skFitSpline(sketch, "E488", {"points": [v(55.2, 1.88) * mm, v(55.2, -0.05) * mm, v(54.97, -1.86) * mm, v(54.53, -3.56) * mm]});
            skFitSpline(sketch, "E489", {"points": [v(54.53, -3.56) * mm, v(54.09, -5.25) * mm, v(53.55, -6.38) * mm, v(52.93, -6.94) * mm]});
            skFitSpline(sketch, "E490", {"points": [v(52.93, -6.94) * mm, v(52.3, -7.5) * mm, v(51.87, -7.78) * mm, v(51.63, -7.78) * mm]});
            skFitSpline(sketch, "E491", {"points": [v(51.63, -7.78) * mm, v(51.22, -7.78) * mm, v(50.7, -7.58) * mm, v(50.08, -7.17) * mm]});
            skFitSpline(sketch, "E492", {"points": [v(50.08, -7.17) * mm, v(49.45, -6.76) * mm, v(48.96, -6.02) * mm, v(48.6, -4.93) * mm]});
            skFitSpline(sketch, "E493", {"points": [v(48.6, -4.93) * mm, v(48.25, -3.85) * mm, v(48.07, -2.64) * mm, v(48.07, -1.32) * mm]});
            skFitSpline(sketch, "E494", {"points": [v(48.07, -1.32) * mm, v(48.07, -0.3) * mm, v(48.16, 0.46) * mm, v(48.33, 0.97) * mm]});
            skFitSpline(sketch, "E495", {"points": [v(67.24, 8.6) * mm, v(65.65, 8.05) * mm, v(64.5, 7.42) * mm, v(63.78, 6.7) * mm]});
            skFitSpline(sketch, "E496", {"points": [v(63.78, 6.7) * mm, v(63.07, 5.97) * mm, v(62.38, 4.44) * mm, v(61.7, 2.1) * mm]});
            skFitSpline(sketch, "E497", {"points": [v(61.7, 2.1) * mm, v(61.02, -0.23) * mm, v(60.68, -2.16) * mm, v(60.68, -3.68) * mm]});
            skFitSpline(sketch, "E498", {"points": [v(60.68, -3.68) * mm, v(60.68, -5.57) * mm, v(61.07, -7.2) * mm, v(61.85, -8.55) * mm]});
            skFitSpline(sketch, "E499", {"points": [v(61.85, -8.55) * mm, v(62.63, -9.9) * mm, v(63.71, -10.58) * mm, v(65.1, -10.58) * mm]});
            skFitSpline(sketch, "E500", {"points": [v(65.1, -10.58) * mm, v(66.53, -10.58) * mm, v(67.9, -10.12) * mm, v(69.22, -9.2) * mm]});
            skFitSpline(sketch, "E501", {"points": [v(71.82, -7.53) * mm, v(72.3, -7.23) * mm, v(72.7, -6.93) * mm, v(73.04, -6.65) * mm]});
            skFitSpline(sketch, "E502", {"points": [v(73.04, -6.65) * mm, v(73.37, -6.36) * mm, v(73.71, -6.05) * mm, v(74.05, -5.7) * mm]});
            skFitSpline(sketch, "E503", {"points": [v(74.05, -5.7) * mm, v(74.4, -5.37) * mm, v(74.65, -4.8) * mm, v(74.82, -3.98) * mm]});
            skFitSpline(sketch, "E504", {"points": [v(76.19, 3.12) * mm, v(76.19, 4.64) * mm, v(75.55, 6.1) * mm, v(74.28, 7.5) * mm]});
            skFitSpline(sketch, "E505", {"points": [v(74.28, 7.5) * mm, v(73.01, 8.9) * mm, v(71.92, 9.6) * mm, v(71, 9.6) * mm]});
            skFitSpline(sketch, "E506", {"points": [v(66.27, 5.19) * mm, v(66.51, 5.86) * mm, v(66.77, 6.39) * mm, v(67.04, 6.76) * mm]});
            skFitSpline(sketch, "E507", {"points": [v(67.04, 6.76) * mm, v(67.38, 7.1) * mm, v(67.62, 7.32) * mm, v(67.77, 7.42) * mm]});
            skFitSpline(sketch, "E508", {"points": [v(67.77, 7.42) * mm, v(67.93, 7.52) * mm, v(68.11, 7.65) * mm, v(68.33, 7.8) * mm]});
            skFitSpline(sketch, "E509", {"points": [v(68.33, 7.8) * mm, v(68.55, 7.96) * mm, v(68.82, 8.03) * mm, v(69.12, 8.03) * mm]});
            skFitSpline(sketch, "E510", {"points": [v(69.12, 8.03) * mm, v(69.7, 8.03) * mm, v(70.21, 7.75) * mm, v(70.67, 7.2) * mm]});
            skFitSpline(sketch, "E511", {"points": [v(70.67, 7.2) * mm, v(71.13, 6.63) * mm, v(71.4, 6.03) * mm, v(71.51, 5.39) * mm]});
            skFitSpline(sketch, "E512", {"points": [v(71.51, 5.39) * mm, v(71.78, 4.2) * mm, v(71.92, 3.03) * mm, v(71.92, 1.88) * mm]});
            skFitSpline(sketch, "E513", {"points": [v(71.92, 1.88) * mm, v(71.92, -0.05) * mm, v(71.7, -1.86) * mm, v(71.26, -3.56) * mm]});
            skFitSpline(sketch, "E514", {"points": [v(71.26, -3.56) * mm, v(70.82, -5.25) * mm, v(70.28, -6.38) * mm, v(69.66, -6.94) * mm]});
            skFitSpline(sketch, "E515", {"points": [v(69.66, -6.94) * mm, v(69.03, -7.5) * mm, v(68.6, -7.78) * mm, v(68.36, -7.78) * mm]});
            skFitSpline(sketch, "E516", {"points": [v(68.36, -7.78) * mm, v(67.95, -7.78) * mm, v(67.44, -7.58) * mm, v(66.8, -7.17) * mm]});
            skFitSpline(sketch, "E517", {"points": [v(66.8, -7.17) * mm, v(66.18, -6.76) * mm, v(65.69, -6.02) * mm, v(65.33, -4.93) * mm]});
            skFitSpline(sketch, "E518", {"points": [v(65.33, -4.93) * mm, v(64.98, -3.85) * mm, v(64.8, -2.64) * mm, v(64.8, -1.32) * mm]});
            skFitSpline(sketch, "E519", {"points": [v(64.8, -1.32) * mm, v(64.8, -0.3) * mm, v(64.88, 0.46) * mm, v(65.05, 0.97) * mm]});
            skFitSpline(sketch, "E520", {"points": [v(79.65, 4.78) * mm, v(79.75, 5.5) * mm, v(80.04, 5.92) * mm, v(80.54, 6.08) * mm]});
            skFitSpline(sketch, "E521", {"points": [v(80.54, 6.08) * mm, v(81.03, 6.23) * mm, v(81.9, 6.3) * mm, v(83.16, 6.3) * mm]});
            skFitSpline(sketch, "E522", {"points": [v(87.83, 6.4) * mm, v(87.02, 4.64) * mm, v(85.94, 2.7) * mm, v(84.6, 0.56) * mm]});
            skFitSpline(sketch, "E523", {"points": [v(84.6, 0.56) * mm, v(83.27, -1.58) * mm, v(81.98, -3.37) * mm, v(80.74, -4.83) * mm]});
            skFitSpline(sketch, "E524", {"points": [v(80.74, -4.83) * mm, v(79.5, -6.29) * mm, v(77.88, -7.88) * mm, v(75.88, -9.6) * mm]});
            skFitSpline(sketch, "E525", {"points": [v(76.65, -10.42) * mm, v(77.77, -9.58) * mm, v(79.3, -8.29) * mm, v(81.25, -6.56) * mm]});
            skFitSpline(sketch, "E526", {"points": [v(81.25, -6.56) * mm, v(83.2, -4.83) * mm, v(85, -2.78) * mm, v(86.66, -0.4) * mm]});
            skFitSpline(sketch, "E527", {"points": [v(92.2, 8.9) * mm, v(92.27, 9) * mm, v(92.3, 9.15) * mm, v(92.3, 9.36) * mm]});
            skFitSpline(sketch, "E528", {"points": [v(92.3, 9.36) * mm, v(92.3, 9.6) * mm, v(92.19, 9.71) * mm, v(91.95, 9.71) * mm]});
            skFitSpline(sketch, "E529", {"points": [v(91.54, 9.56) * mm, v(91.14, 9.25) * mm, v(90.4, 9.1) * mm, v(89.3, 9.1) * mm]});
            skFitSpline(sketch, "E530", {"points": [v(82.04, 9.97) * mm, v(81.15, 9.97) * mm, v(80.46, 9.81) * mm, v(79.95, 9.5) * mm]});
            skFitSpline(sketch, "E531", {"points": [v(79.95, 9.5) * mm, v(79.44, 9.2) * mm, v(79.11, 8.86) * mm, v(78.96, 8.5) * mm]});
            skFitSpline(sketch, "E532", {"points": [v(78.96, 8.5) * mm, v(78.8, 8.12) * mm, v(78.7, 7.64) * mm, v(78.63, 7.07) * mm]});
            skFitSpline(sketch, "E533", {"points": [v(78.43, 5.34) * mm, v(78.43, 4.25) * mm, v(78.61, 3.71) * mm, v(78.99, 3.71) * mm]});
            skFitSpline(sketch, "E534", {"points": [v(78.99, 3.71) * mm, v(79.32, 3.71) * mm, v(79.54, 4.07) * mm, v(79.65, 4.78) * mm]});
            skFitSpline(sketch, "E535", {"points": [v(76.34, -10.02) * mm, v(76.4, -10.08) * mm, v(76.56, -10.17) * mm, v(76.8, -10.27) * mm]});
            skFitSpline(sketch, "E536", {"points": [v(79.09, -8.5) * mm, v(79.56, -8.19) * mm, v(80, -8.03) * mm, v(80.4, -8.03) * mm]});
            skFitSpline(sketch, "E537", {"points": [v(80.4, -8.03) * mm, v(81.05, -8.03) * mm, v(82.09, -8.55) * mm, v(83.51, -9.58) * mm]});
            skFitSpline(sketch, "E538", {"points": [v(83.51, -9.58) * mm, v(84.32, -10.24) * mm, v(85.26, -10.58) * mm, v(86.3, -10.58) * mm]});
            skFitSpline(sketch, "E539", {"points": [v(86.3, -10.58) * mm, v(87.36, -10.58) * mm, v(88.37, -10.22) * mm, v(89.36, -9.52) * mm]});
            skFitSpline(sketch, "E540", {"points": [v(89.36, -9.52) * mm, v(90.34, -8.81) * mm, v(91.04, -8.05) * mm, v(91.44, -7.23) * mm]});
            skFitSpline(sketch, "E541", {"points": [v(91.44, -7.23) * mm, v(91.85, -6.4) * mm, v(92.05, -5.82) * mm, v(92.05, -5.49) * mm]});
            skFitSpline(sketch, "E542", {"points": [v(92.05, -5.49) * mm, v(92.05, -5.35) * mm, v(91.97, -5.22) * mm, v(91.8, -5.09) * mm]});
            skFitSpline(sketch, "E543", {"points": [v(91.8, -5.09) * mm, v(91.5, -5.09) * mm, v(91.24, -5.3) * mm, v(91.04, -5.75) * mm]});
            skFitSpline(sketch, "E544", {"points": [v(91.04, -5.75) * mm, v(90.32, -6.8) * mm, v(89.46, -7.32) * mm, v(88.44, -7.32) * mm]});
            skFitSpline(sketch, "E545", {"points": [v(88.44, -7.32) * mm, v(88.1, -7.32) * mm, v(87.79, -7.29) * mm, v(87.5, -7.22) * mm]});
            skFitSpline(sketch, "E546", {"points": [v(87.5, -7.22) * mm, v(87.21, -7.15) * mm, v(86.9, -7.05) * mm, v(86.56, -6.92) * mm]});
            skFitSpline(sketch, "E547", {"points": [v(81.58, -4.63) * mm, v(81.27, -4.5) * mm, v(80.93, -4.42) * mm, v(80.56, -4.42) * mm]});
            skFitSpline(sketch, "E548", {"points": [v(80.56, -4.42) * mm, v(79.68, -4.42) * mm, v(78.88, -4.79) * mm, v(78.15, -5.52) * mm]});
            skFitSpline(sketch, "E549", {"points": [v(78.15, -5.52) * mm, v(77.42, -6.25) * mm, v(76.93, -7.07) * mm, v(76.7, -7.98) * mm]});
            skFitSpline(sketch, "E550", {"points": [v(106.6, 7.08) * mm, v(106.86, 7.22) * mm, v(107.1, 7.45) * mm, v(107.28, 7.78) * mm]});
            skFitSpline(sketch, "E551", {"points": [v(107.28, 7.78) * mm, v(107.47, 8.11) * mm, v(107.56, 8.42) * mm, v(107.56, 8.7) * mm]});
            skFitSpline(sketch, "E552", {"points": [v(107.56, 8.7) * mm, v(107.56, 9.2) * mm, v(107.05, 9.47) * mm, v(106.03, 9.47) * mm]});
            skFitSpline(sketch, "E553", {"points": [v(102.17, 9.11) * mm, v(101.25, 9.11) * mm, v(100.39, 8.9) * mm, v(99.58, 8.48) * mm]});
            skFitSpline(sketch, "E554", {"points": [v(99.58, 8.48) * mm, v(98.76, 8.05) * mm, v(97.86, 7.3) * mm, v(96.88, 6.24) * mm]});
            skFitSpline(sketch, "E555", {"points": [v(96.88, 6.24) * mm, v(95.9, 5.17) * mm, v(95.14, 3.92) * mm, v(94.6, 2.48) * mm]});
            skFitSpline(sketch, "E556", {"points": [v(94.6, 2.48) * mm, v(94.05, 1.04) * mm, v(93.66, -0.14) * mm, v(93.42, -1.06) * mm]});
            skFitSpline(sketch, "E557", {"points": [v(93.42, -1.06) * mm, v(93.19, -1.97) * mm, v(93, -2.8) * mm, v(92.9, -3.55) * mm]});
            skFitSpline(sketch, "E558", {"points": [v(92.9, -3.55) * mm, v(92.77, -4.3) * mm, v(92.7, -4.91) * mm, v(92.66, -5.4) * mm]});
            skFitSpline(sketch, "E559", {"points": [v(92.66, -5.4) * mm, v(92.63, -5.9) * mm, v(92.61, -6.26) * mm, v(92.61, -6.5) * mm]});
            skFitSpline(sketch, "E560", {"points": [v(92.61, -6.5) * mm, v(92.61, -9.17) * mm, v(93.36, -10.51) * mm, v(94.85, -10.51) * mm]});
            skFitSpline(sketch, "E561", {"points": [v(94.85, -10.51) * mm, v(96.24, -10.51) * mm, v(98.17, -9.22) * mm, v(100.65, -6.63) * mm]});
            skFitSpline(sketch, "E562", {"points": [v(102.37, -4.74) * mm, v(102.91, -4.2) * mm, v(103.36, -3.63) * mm, v(103.7, -3.05) * mm]});
            skFitSpline(sketch, "E563", {"points": [v(103.7, -3.05) * mm, v(104.03, -2.47) * mm, v(104.2, -1.9) * mm, v(104.2, -1.31) * mm]});
            skFitSpline(sketch, "E564", {"points": [v(104.2, -1.31) * mm, v(104.2, -1.14) * mm, v(104.14, -0.94) * mm, v(104, -0.7) * mm]});
            skFitSpline(sketch, "E565", {"points": [v(102.83, -2.13) * mm, v(102.12, -3.13) * mm, v(101.27, -4.14) * mm, v(100.29, -5.19) * mm]});
            skFitSpline(sketch, "E566", {"points": [v(100.29, -5.19) * mm, v(99.3, -6.23) * mm, v(98.46, -6.75) * mm, v(97.75, -6.75) * mm]});
            skFitSpline(sketch, "E567", {"points": [v(97.75, -6.75) * mm, v(96.9, -6.75) * mm, v(96.47, -5.85) * mm, v(96.47, -4.05) * mm]});
            skFitSpline(sketch, "E568", {"points": [v(96.47, -4.05) * mm, v(96.47, -2.8) * mm, v(96.65, -1.25) * mm, v(97, 0.6) * mm]});
            skFitSpline(sketch, "E569", {"points": [v(97, 0.6) * mm, v(97.36, 2.44) * mm, v(97.77, 3.8) * mm, v(98.23, 4.69) * mm]});
            skFitSpline(sketch, "E570", {"points": [v(98.23, 4.69) * mm, v(98.69, 5.57) * mm, v(99.18, 6.16) * mm, v(99.7, 6.44) * mm]});
            skFitSpline(sketch, "E571", {"points": [v(99.7, 6.44) * mm, v(100.23, 6.73) * mm, v(100.83, 6.88) * mm, v(101.5, 6.88) * mm]});
            skFitSpline(sketch, "E572", {"points": [v(107.85, 7.58) * mm, v(107.85, 8.76) * mm, v(107.48, 9.36) * mm, v(106.74, 9.36) * mm]});
            skFitSpline(sketch, "E573", {"points": [v(106.74, 9.36) * mm, v(106.33, 9.36) * mm, v(105.84, 9.12) * mm, v(105.27, 8.64) * mm]});
            skFitSpline(sketch, "E574", {"points": [v(105.27, 8.64) * mm, v(104.76, 8.13) * mm, v(104.35, 7.48) * mm, v(104.03, 6.68) * mm]});
            skFitSpline(sketch, "E575", {"points": [v(104.03, 6.68) * mm, v(103.71, 5.89) * mm, v(103.48, 5.2) * mm, v(103.35, 4.6) * mm]});
            skFitSpline(sketch, "E576", {"points": [v(103.35, 4.6) * mm, v(103.21, 4) * mm, v(103.11, 3.29) * mm, v(103.05, 2.44) * mm]});
            skFitSpline(sketch, "E577", {"points": [v(101.81, -8.6) * mm, v(101.81, -9.85) * mm, v(102.1, -10.47) * mm, v(102.68, -10.47) * mm]});
            skFitSpline(sketch, "E578", {"points": [v(102.68, -10.47) * mm, v(103.22, -10.47) * mm, v(103.97, -10.1) * mm, v(104.92, -9.36) * mm]});
            skFitSpline(sketch, "E579", {"points": [v(104.92, -9.36) * mm, v(105.86, -8.71) * mm, v(107.4, -7.44) * mm, v(109.54, -5.54) * mm]});
            skFitSpline(sketch, "E580", {"points": [v(109.54, -5.54) * mm, v(109.68, -5.37) * mm, v(109.78, -5.24) * mm, v(109.85, -5.13) * mm]});
            skFitSpline(sketch, "E581", {"points": [v(109.85, -5.13) * mm, v(109.91, -5.03) * mm, v(109.97, -4.93) * mm, v(110, -4.83) * mm]});
            skFitSpline(sketch, "E582", {"points": [v(110, -4.83) * mm, v(110, -4.76) * mm, v(109.91, -4.68) * mm, v(109.75, -4.58) * mm]});
            skFitSpline(sketch, "E583", {"points": [v(109.75, -4.58) * mm, v(109.5, -4.58) * mm, v(109.21, -4.7) * mm, v(108.86, -4.93) * mm]});
            skFitSpline(sketch, "E584", {"points": [v(108.86, -4.93) * mm, v(108.5, -5.17) * mm, v(108.17, -5.4) * mm, v(107.86, -5.64) * mm]});
            skFitSpline(sketch, "E585", {"points": [v(107.86, -5.64) * mm, v(107.56, -5.88) * mm, v(107.29, -6.12) * mm, v(107.05, -6.36) * mm]});
            skFitSpline(sketch, "E586", {"points": [v(105.98, -7.12) * mm, v(105.95, -7.09) * mm, v(105.9, -7.03) * mm, v(105.86, -6.94) * mm]});
            skFitSpline(sketch, "E587", {"points": [v(105.86, -6.94) * mm, v(105.8, -6.86) * mm, v(105.78, -6.71) * mm, v(105.78, -6.5) * mm]});
            skSolve(sketch);
        }
        {
            var Q0;
            Q0 = qSketchRegion(id + "F2", true);
            extrude(context, id + "F3", {"entities" : qUnion([Q0]), "operationType" : NewBodyOperationType.ADD, "depth" : 1 * mm, "offsetDistance" : 25 * mm});
        }
    });
